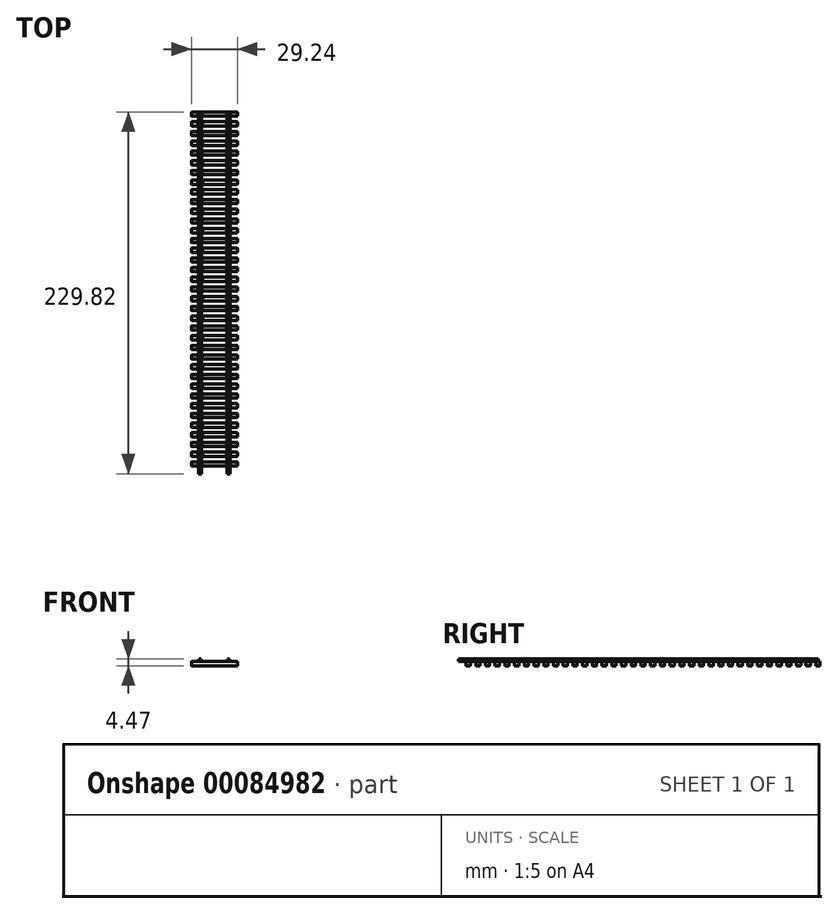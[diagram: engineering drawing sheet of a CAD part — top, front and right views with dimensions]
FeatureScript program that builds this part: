
annotation { "Feature Type Name" : "Feature", "Feature Type Description" : "" }
export const myFeature = defineFeature(function(context is Context, id is Id, definition is map)
    precondition{}
    {
        {
            var Q0;
            Q0=qCreatedBy(makeId("Top.planeOp"),FACE);
            var sketch = newSketch(context, id + "F0", { "sketchPlane" : qUnion([Q0])});
            skLineSegment(sketch, "E0.bottom", {"start": v(-14.62, 0) * mm, "end": v(14.62, 0) * mm});
            skLineSegment(sketch, "E0.top", {"start": v(-14.62, -2.7) * mm, "end": v(14.62, -2.7) * mm});
            skLineSegment(sketch, "E0.left", {"start": v(-14.62, 0) * mm, "end": v(-14.62, -2.7) * mm});
            skLineSegment(sketch, "E0.right", {"start": v(14.62, 0) * mm, "end": v(14.62, -2.7) * mm});
            skLineSegment(sketch, "E1.0.1.0", {"start": v(-14.62, 3.48) * mm, "end": v(14.62, 3.48) * mm});
            skLineSegment(sketch, "E1.0.1.1", {"start": v(-14.62, 6.17) * mm, "end": v(14.62, 6.17) * mm});
            skLineSegment(sketch, "E1.0.1.2", {"start": v(-14.62, 6.17) * mm, "end": v(-14.62, 3.48) * mm});
            skLineSegment(sketch, "E1.0.1.3", {"start": v(14.62, 6.17) * mm, "end": v(14.62, 3.48) * mm});
            skLineSegment(sketch, "E1.0.2.0", {"start": v(-14.62, 9.65) * mm, "end": v(14.62, 9.65) * mm});
            skLineSegment(sketch, "E1.0.2.1", {"start": v(-14.62, 12.34) * mm, "end": v(14.62, 12.34) * mm});
            skLineSegment(sketch, "E1.0.2.2", {"start": v(-14.62, 12.34) * mm, "end": v(-14.62, 9.65) * mm});
            skLineSegment(sketch, "E1.0.2.3", {"start": v(14.62, 12.34) * mm, "end": v(14.62, 9.65) * mm});
            skLineSegment(sketch, "E1.0.3.0", {"start": v(-14.62, 15.82) * mm, "end": v(14.62, 15.82) * mm});
            skLineSegment(sketch, "E1.0.3.1", {"start": v(-14.62, 18.52) * mm, "end": v(14.62, 18.52) * mm});
            skLineSegment(sketch, "E1.0.3.2", {"start": v(-14.62, 18.52) * mm, "end": v(-14.62, 15.82) * mm});
            skLineSegment(sketch, "E1.0.3.3", {"start": v(14.62, 18.52) * mm, "end": v(14.62, 15.82) * mm});
            skLineSegment(sketch, "E1.0.4.0", {"start": v(-14.62, 22) * mm, "end": v(14.62, 22) * mm});
            skLineSegment(sketch, "E1.0.4.1", {"start": v(-14.62, 24.69) * mm, "end": v(14.62, 24.69) * mm});
            skLineSegment(sketch, "E1.0.4.2", {"start": v(-14.62, 24.69) * mm, "end": v(-14.62, 22) * mm});
            skLineSegment(sketch, "E1.0.4.3", {"start": v(14.62, 24.69) * mm, "end": v(14.62, 22) * mm});
            skLineSegment(sketch, "E1.0.5.0", {"start": v(-14.62, 28.17) * mm, "end": v(14.62, 28.17) * mm});
            skLineSegment(sketch, "E1.0.5.1", {"start": v(-14.62, 30.86) * mm, "end": v(14.62, 30.86) * mm});
            skLineSegment(sketch, "E1.0.5.2", {"start": v(-14.62, 30.86) * mm, "end": v(-14.62, 28.17) * mm});
            skLineSegment(sketch, "E1.0.5.3", {"start": v(14.62, 30.86) * mm, "end": v(14.62, 28.17) * mm});
            skLineSegment(sketch, "E1.0.6.0", {"start": v(-14.62, 34.34) * mm, "end": v(14.62, 34.34) * mm});
            skLineSegment(sketch, "E1.0.6.1", {"start": v(-14.62, 37.03) * mm, "end": v(14.62, 37.03) * mm});
            skLineSegment(sketch, "E1.0.6.2", {"start": v(-14.62, 37.03) * mm, "end": v(-14.62, 34.34) * mm});
            skLineSegment(sketch, "E1.0.6.3", {"start": v(14.62, 37.03) * mm, "end": v(14.62, 34.34) * mm});
            skLineSegment(sketch, "E1.0.7.0", {"start": v(-14.62, 40.51) * mm, "end": v(14.62, 40.51) * mm});
            skLineSegment(sketch, "E1.0.7.1", {"start": v(-14.62, 43.2) * mm, "end": v(14.62, 43.2) * mm});
            skLineSegment(sketch, "E1.0.7.2", {"start": v(-14.62, 43.2) * mm, "end": v(-14.62, 40.51) * mm});
            skLineSegment(sketch, "E1.0.7.3", {"start": v(14.62, 43.2) * mm, "end": v(14.62, 40.51) * mm});
            skLineSegment(sketch, "E1.0.8.0", {"start": v(-14.62, 46.69) * mm, "end": v(14.62, 46.69) * mm});
            skLineSegment(sketch, "E1.0.8.1", {"start": v(-14.62, 49.38) * mm, "end": v(14.62, 49.38) * mm});
            skLineSegment(sketch, "E1.0.8.2", {"start": v(-14.62, 49.38) * mm, "end": v(-14.62, 46.69) * mm});
            skLineSegment(sketch, "E1.0.8.3", {"start": v(14.62, 49.38) * mm, "end": v(14.62, 46.69) * mm});
            skLineSegment(sketch, "E1.0.9.0", {"start": v(-14.62, 52.86) * mm, "end": v(14.62, 52.86) * mm});
            skLineSegment(sketch, "E1.0.9.1", {"start": v(-14.62, 55.55) * mm, "end": v(14.62, 55.55) * mm});
            skLineSegment(sketch, "E1.0.9.2", {"start": v(-14.62, 55.55) * mm, "end": v(-14.62, 52.86) * mm});
            skLineSegment(sketch, "E1.0.9.3", {"start": v(14.62, 55.55) * mm, "end": v(14.62, 52.86) * mm});
            skLineSegment(sketch, "E1.0.10.0", {"start": v(-14.62, 59.03) * mm, "end": v(14.62, 59.03) * mm});
            skLineSegment(sketch, "E1.0.10.1", {"start": v(-14.62, 61.72) * mm, "end": v(14.62, 61.72) * mm});
            skLineSegment(sketch, "E1.0.10.2", {"start": v(-14.62, 61.72) * mm, "end": v(-14.62, 59.03) * mm});
            skLineSegment(sketch, "E1.0.10.3", {"start": v(14.62, 61.72) * mm, "end": v(14.62, 59.03) * mm});
            skLineSegment(sketch, "E1.0.11.0", {"start": v(-14.62, 65.2) * mm, "end": v(14.62, 65.2) * mm});
            skLineSegment(sketch, "E1.0.11.1", {"start": v(-14.62, 67.9) * mm, "end": v(14.62, 67.9) * mm});
            skLineSegment(sketch, "E1.0.11.2", {"start": v(-14.62, 67.9) * mm, "end": v(-14.62, 65.2) * mm});
            skLineSegment(sketch, "E1.0.11.3", {"start": v(14.62, 67.9) * mm, "end": v(14.62, 65.2) * mm});
            skLineSegment(sketch, "E1.0.12.0", {"start": v(-14.62, 71.37) * mm, "end": v(14.62, 71.37) * mm});
            skLineSegment(sketch, "E1.0.12.1", {"start": v(-14.62, 74.07) * mm, "end": v(14.62, 74.07) * mm});
            skLineSegment(sketch, "E1.0.12.2", {"start": v(-14.62, 74.07) * mm, "end": v(-14.62, 71.37) * mm});
            skLineSegment(sketch, "E1.0.12.3", {"start": v(14.62, 74.07) * mm, "end": v(14.62, 71.37) * mm});
            skLineSegment(sketch, "E1.0.13.0", {"start": v(-14.62, 77.55) * mm, "end": v(14.62, 77.55) * mm});
            skLineSegment(sketch, "E1.0.13.1", {"start": v(-14.62, 80.24) * mm, "end": v(14.62, 80.24) * mm});
            skLineSegment(sketch, "E1.0.13.2", {"start": v(-14.62, 80.24) * mm, "end": v(-14.62, 77.55) * mm});
            skLineSegment(sketch, "E1.0.13.3", {"start": v(14.62, 80.24) * mm, "end": v(14.62, 77.55) * mm});
            skLineSegment(sketch, "E1.0.14.0", {"start": v(-14.62, 83.72) * mm, "end": v(14.62, 83.72) * mm});
            skLineSegment(sketch, "E1.0.14.1", {"start": v(-14.62, 86.41) * mm, "end": v(14.62, 86.41) * mm});
            skLineSegment(sketch, "E1.0.14.2", {"start": v(-14.62, 86.41) * mm, "end": v(-14.62, 83.72) * mm});
            skLineSegment(sketch, "E1.0.14.3", {"start": v(14.62, 86.41) * mm, "end": v(14.62, 83.72) * mm});
            skLineSegment(sketch, "E1.0.15.0", {"start": v(-14.62, 89.9) * mm, "end": v(14.62, 89.9) * mm});
            skLineSegment(sketch, "E1.0.15.1", {"start": v(-14.62, 92.58) * mm, "end": v(14.62, 92.58) * mm});
            skLineSegment(sketch, "E1.0.15.2", {"start": v(-14.62, 92.58) * mm, "end": v(-14.62, 89.9) * mm});
            skLineSegment(sketch, "E1.0.15.3", {"start": v(14.62, 92.58) * mm, "end": v(14.62, 89.9) * mm});
            skLineSegment(sketch, "E1.0.16.0", {"start": v(-14.62, 96.06) * mm, "end": v(14.62, 96.06) * mm});
            skLineSegment(sketch, "E1.0.16.1", {"start": v(-14.62, 98.76) * mm, "end": v(14.62, 98.76) * mm});
            skLineSegment(sketch, "E1.0.16.2", {"start": v(-14.62, 98.76) * mm, "end": v(-14.62, 96.06) * mm});
            skLineSegment(sketch, "E1.0.16.3", {"start": v(14.62, 98.76) * mm, "end": v(14.62, 96.06) * mm});
            skLineSegment(sketch, "E1.0.17.0", {"start": v(-14.62, 102.23) * mm, "end": v(14.62, 102.23) * mm});
            skLineSegment(sketch, "E1.0.17.1", {"start": v(-14.62, 104.93) * mm, "end": v(14.62, 104.93) * mm});
            skLineSegment(sketch, "E1.0.17.2", {"start": v(-14.62, 104.93) * mm, "end": v(-14.62, 102.23) * mm});
            skLineSegment(sketch, "E1.0.17.3", {"start": v(14.62, 104.93) * mm, "end": v(14.62, 102.23) * mm});
            skLineSegment(sketch, "E1.0.18.0", {"start": v(-14.62, 108.4) * mm, "end": v(14.62, 108.4) * mm});
            skLineSegment(sketch, "E1.0.18.1", {"start": v(-14.62, 111.1) * mm, "end": v(14.62, 111.1) * mm});
            skLineSegment(sketch, "E1.0.18.2", {"start": v(-14.62, 111.1) * mm, "end": v(-14.62, 108.4) * mm});
            skLineSegment(sketch, "E1.0.18.3", {"start": v(14.62, 111.1) * mm, "end": v(14.62, 108.4) * mm});
            skLineSegment(sketch, "E1.0.19.0", {"start": v(-14.62, 114.58) * mm, "end": v(14.62, 114.58) * mm});
            skLineSegment(sketch, "E1.0.19.1", {"start": v(-14.62, 117.27) * mm, "end": v(14.62, 117.27) * mm});
            skLineSegment(sketch, "E1.0.19.2", {"start": v(-14.62, 117.27) * mm, "end": v(-14.62, 114.58) * mm});
            skLineSegment(sketch, "E1.0.19.3", {"start": v(14.62, 117.27) * mm, "end": v(14.62, 114.58) * mm});
            skLineSegment(sketch, "E1.direction1", {"start": v(-14.62, -2.7) * mm, "end": v(10.4, -2.7) * mm, "construction": true});
            skLineSegment(sketch, "E1.direction2", {"start": v(-14.62, -2.7) * mm, "end": v(-14.62, 3.48) * mm, "construction": true});
            skLineSegment(sketch, "E2.0.0.20", {"start": v(-14.62, 120.75) * mm, "end": v(14.62, 120.75) * mm});
            skLineSegment(sketch, "E2.3.0.20", {"start": v(-14.62, 123.44) * mm, "end": v(14.62, 123.44) * mm});
            skLineSegment(sketch, "E2.6.0.20", {"start": v(-14.62, 123.44) * mm, "end": v(-14.62, 120.75) * mm});
            skLineSegment(sketch, "E2.9.0.20", {"start": v(14.62, 123.44) * mm, "end": v(14.62, 120.75) * mm});
            skLineSegment(sketch, "E2.0.0.21", {"start": v(-14.62, 126.92) * mm, "end": v(14.62, 126.92) * mm});
            skLineSegment(sketch, "E2.3.0.21", {"start": v(-14.62, 129.62) * mm, "end": v(14.62, 129.62) * mm});
            skLineSegment(sketch, "E2.6.0.21", {"start": v(-14.62, 129.62) * mm, "end": v(-14.62, 126.92) * mm});
            skLineSegment(sketch, "E2.9.0.21", {"start": v(14.62, 129.62) * mm, "end": v(14.62, 126.92) * mm});
            skLineSegment(sketch, "E2.0.0.22", {"start": v(-14.62, 133.1) * mm, "end": v(14.62, 133.1) * mm});
            skLineSegment(sketch, "E2.3.0.22", {"start": v(-14.62, 135.79) * mm, "end": v(14.62, 135.79) * mm});
            skLineSegment(sketch, "E2.6.0.22", {"start": v(-14.62, 135.79) * mm, "end": v(-14.62, 133.1) * mm});
            skLineSegment(sketch, "E2.9.0.22", {"start": v(14.62, 135.79) * mm, "end": v(14.62, 133.1) * mm});
            skLineSegment(sketch, "E2.0.0.23", {"start": v(-14.62, 139.27) * mm, "end": v(14.62, 139.27) * mm});
            skLineSegment(sketch, "E2.3.0.23", {"start": v(-14.62, 141.96) * mm, "end": v(14.62, 141.96) * mm});
            skLineSegment(sketch, "E2.6.0.23", {"start": v(-14.62, 141.96) * mm, "end": v(-14.62, 139.27) * mm});
            skLineSegment(sketch, "E2.9.0.23", {"start": v(14.62, 141.96) * mm, "end": v(14.62, 139.27) * mm});
            skLineSegment(sketch, "E2.0.0.24", {"start": v(-14.62, 145.44) * mm, "end": v(14.62, 145.44) * mm});
            skLineSegment(sketch, "E2.3.0.24", {"start": v(-14.62, 148.13) * mm, "end": v(14.62, 148.13) * mm});
            skLineSegment(sketch, "E2.6.0.24", {"start": v(-14.62, 148.13) * mm, "end": v(-14.62, 145.44) * mm});
            skLineSegment(sketch, "E2.9.0.24", {"start": v(14.62, 148.13) * mm, "end": v(14.62, 145.44) * mm});
            skLineSegment(sketch, "E2.0.0.25", {"start": v(-14.62, 151.61) * mm, "end": v(14.62, 151.61) * mm});
            skLineSegment(sketch, "E2.3.0.25", {"start": v(-14.62, 154.3) * mm, "end": v(14.62, 154.3) * mm});
            skLineSegment(sketch, "E2.6.0.25", {"start": v(-14.62, 154.3) * mm, "end": v(-14.62, 151.61) * mm});
            skLineSegment(sketch, "E2.9.0.25", {"start": v(14.62, 154.3) * mm, "end": v(14.62, 151.61) * mm});
            skLineSegment(sketch, "E2.0.0.26", {"start": v(-14.62, 157.78) * mm, "end": v(14.62, 157.78) * mm});
            skLineSegment(sketch, "E2.3.0.26", {"start": v(-14.62, 160.48) * mm, "end": v(14.62, 160.48) * mm});
            skLineSegment(sketch, "E2.6.0.26", {"start": v(-14.62, 160.48) * mm, "end": v(-14.62, 157.78) * mm});
            skLineSegment(sketch, "E2.9.0.26", {"start": v(14.62, 160.48) * mm, "end": v(14.62, 157.78) * mm});
            skLineSegment(sketch, "E2.0.0.27", {"start": v(-14.62, 163.96) * mm, "end": v(14.62, 163.96) * mm});
            skLineSegment(sketch, "E2.3.0.27", {"start": v(-14.62, 166.65) * mm, "end": v(14.62, 166.65) * mm});
            skLineSegment(sketch, "E2.6.0.27", {"start": v(-14.62, 166.65) * mm, "end": v(-14.62, 163.96) * mm});
            skLineSegment(sketch, "E2.9.0.27", {"start": v(14.62, 166.65) * mm, "end": v(14.62, 163.96) * mm});
            skLineSegment(sketch, "E2.0.0.28", {"start": v(-14.62, 170.13) * mm, "end": v(14.62, 170.13) * mm});
            skLineSegment(sketch, "E2.3.0.28", {"start": v(-14.62, 172.82) * mm, "end": v(14.62, 172.82) * mm});
            skLineSegment(sketch, "E2.6.0.28", {"start": v(-14.62, 172.82) * mm, "end": v(-14.62, 170.13) * mm});
            skLineSegment(sketch, "E2.9.0.28", {"start": v(14.62, 172.82) * mm, "end": v(14.62, 170.13) * mm});
            skLineSegment(sketch, "E2.0.0.29", {"start": v(-14.62, 176.3) * mm, "end": v(14.62, 176.3) * mm});
            skLineSegment(sketch, "E2.3.0.29", {"start": v(-14.62, 179) * mm, "end": v(14.62, 179) * mm});
            skLineSegment(sketch, "E2.6.0.29", {"start": v(-14.62, 179) * mm, "end": v(-14.62, 176.3) * mm});
            skLineSegment(sketch, "E2.9.0.29", {"start": v(14.62, 179) * mm, "end": v(14.62, 176.3) * mm});
            skLineSegment(sketch, "E3.0.0.30", {"start": v(-14.62, 182.47) * mm, "end": v(14.62, 182.47) * mm});
            skLineSegment(sketch, "E3.3.0.30", {"start": v(-14.62, 185.17) * mm, "end": v(14.62, 185.17) * mm});
            skLineSegment(sketch, "E3.6.0.30", {"start": v(-14.62, 185.17) * mm, "end": v(-14.62, 182.47) * mm});
            skLineSegment(sketch, "E3.9.0.30", {"start": v(14.62, 185.17) * mm, "end": v(14.62, 182.47) * mm});
            skLineSegment(sketch, "E3.0.0.31", {"start": v(-14.62, 188.65) * mm, "end": v(14.62, 188.65) * mm});
            skLineSegment(sketch, "E3.3.0.31", {"start": v(-14.62, 191.34) * mm, "end": v(14.62, 191.34) * mm});
            skLineSegment(sketch, "E3.6.0.31", {"start": v(-14.62, 191.34) * mm, "end": v(-14.62, 188.65) * mm});
            skLineSegment(sketch, "E3.9.0.31", {"start": v(14.62, 191.34) * mm, "end": v(14.62, 188.65) * mm});
            skLineSegment(sketch, "E3.0.0.32", {"start": v(-14.62, 194.82) * mm, "end": v(14.62, 194.82) * mm});
            skLineSegment(sketch, "E3.3.0.32", {"start": v(-14.62, 197.51) * mm, "end": v(14.62, 197.51) * mm});
            skLineSegment(sketch, "E3.6.0.32", {"start": v(-14.62, 197.51) * mm, "end": v(-14.62, 194.82) * mm});
            skLineSegment(sketch, "E3.9.0.32", {"start": v(14.62, 197.51) * mm, "end": v(14.62, 194.82) * mm});
            skLineSegment(sketch, "E3.0.0.33", {"start": v(-14.62, 201) * mm, "end": v(14.62, 201) * mm});
            skLineSegment(sketch, "E3.3.0.33", {"start": v(-14.62, 203.68) * mm, "end": v(14.62, 203.68) * mm});
            skLineSegment(sketch, "E3.6.0.33", {"start": v(-14.62, 203.68) * mm, "end": v(-14.62, 201) * mm});
            skLineSegment(sketch, "E3.9.0.33", {"start": v(14.62, 203.68) * mm, "end": v(14.62, 201) * mm});
            skLineSegment(sketch, "E3.0.0.34", {"start": v(-14.62, 207.16) * mm, "end": v(14.62, 207.16) * mm});
            skLineSegment(sketch, "E3.3.0.34", {"start": v(-14.62, 209.85) * mm, "end": v(14.62, 209.85) * mm});
            skLineSegment(sketch, "E3.6.0.34", {"start": v(-14.62, 209.85) * mm, "end": v(-14.62, 207.16) * mm});
            skLineSegment(sketch, "E3.9.0.34", {"start": v(14.62, 209.85) * mm, "end": v(14.62, 207.16) * mm});
            skLineSegment(sketch, "E3.0.0.35", {"start": v(-14.62, 213.33) * mm, "end": v(14.62, 213.33) * mm});
            skLineSegment(sketch, "E3.3.0.35", {"start": v(-14.62, 216.03) * mm, "end": v(14.62, 216.03) * mm});
            skLineSegment(sketch, "E3.6.0.35", {"start": v(-14.62, 216.03) * mm, "end": v(-14.62, 213.33) * mm});
            skLineSegment(sketch, "E3.9.0.35", {"start": v(14.62, 216.03) * mm, "end": v(14.62, 213.33) * mm});
            skLineSegment(sketch, "E3.0.0.36", {"start": v(-14.62, 219.5) * mm, "end": v(14.62, 219.5) * mm});
            skLineSegment(sketch, "E3.3.0.36", {"start": v(-14.62, 222.2) * mm, "end": v(14.62, 222.2) * mm});
            skLineSegment(sketch, "E3.6.0.36", {"start": v(-14.62, 222.2) * mm, "end": v(-14.62, 219.5) * mm});
            skLineSegment(sketch, "E3.9.0.36", {"start": v(14.62, 222.2) * mm, "end": v(14.62, 219.5) * mm});
            skSolve(sketch);
        }
        {
            var Q0;
            Q0 = qSketchRegion(id + "F0", true);
            extrude(context, id + "F1", {"entities" : qUnion([Q0]), "depth" : 2.7 * mm});
        }
        {
            var Q0;
            Q0=makeQuery(id+"F1.opExtrude","CAP_FACE",FACE,{"disambiguationData":[OSD([sQuery(id+"F0.wireOp",EDGE,"E0.bottom"),sQuery(id+"F0.wireOp",EDGE,"E0.top"),sQuery(id+"F0.wireOp",EDGE,"E0.left"),sQuery(id+"F0.wireOp",EDGE,"E0.right")])],"isStart":false});
            var Q1;
            Q1=makeQuery(id+"F1.opExtrude","CAP_FACE",FACE,{"disambiguationData":[OSD([sQuery(id+"F0.wireOp",EDGE,"E1.0.1.0"),sQuery(id+"F0.wireOp",EDGE,"E1.0.1.1"),sQuery(id+"F0.wireOp",EDGE,"E1.0.1.2"),sQuery(id+"F0.wireOp",EDGE,"E1.0.1.3")])],"isStart":false});
            var Q2;
            Q2=makeQuery(id+"F1.opExtrude","CAP_FACE",FACE,{"disambiguationData":[OSD([sQuery(id+"F0.wireOp",EDGE,"E1.0.2.0"),sQuery(id+"F0.wireOp",EDGE,"E1.0.2.1"),sQuery(id+"F0.wireOp",EDGE,"E1.0.2.2"),sQuery(id+"F0.wireOp",EDGE,"E1.0.2.3")])],"isStart":false});
            var Q3;
            Q3=makeQuery(id+"F1.opExtrude","CAP_FACE",FACE,{"disambiguationData":[OSD([sQuery(id+"F0.wireOp",EDGE,"E1.0.3.0"),sQuery(id+"F0.wireOp",EDGE,"E1.0.3.1"),sQuery(id+"F0.wireOp",EDGE,"E1.0.3.2"),sQuery(id+"F0.wireOp",EDGE,"E1.0.3.3")])],"isStart":false});
            var Q4;
            Q4=makeQuery(id+"F1.opExtrude","CAP_FACE",FACE,{"disambiguationData":[OSD([sQuery(id+"F0.wireOp",EDGE,"E1.0.4.0"),sQuery(id+"F0.wireOp",EDGE,"E1.0.4.1"),sQuery(id+"F0.wireOp",EDGE,"E1.0.4.2"),sQuery(id+"F0.wireOp",EDGE,"E1.0.4.3")])],"isStart":false});
            var Q5;
            Q5=makeQuery(id+"F1.opExtrude","CAP_FACE",FACE,{"disambiguationData":[OSD([sQuery(id+"F0.wireOp",EDGE,"E1.0.5.0"),sQuery(id+"F0.wireOp",EDGE,"E1.0.5.1"),sQuery(id+"F0.wireOp",EDGE,"E1.0.5.2"),sQuery(id+"F0.wireOp",EDGE,"E1.0.5.3")])],"isStart":false});
            var Q6;
            Q6=makeQuery(id+"F1.opExtrude","CAP_FACE",FACE,{"disambiguationData":[OSD([sQuery(id+"F0.wireOp",EDGE,"E1.0.6.0"),sQuery(id+"F0.wireOp",EDGE,"E1.0.6.1"),sQuery(id+"F0.wireOp",EDGE,"E1.0.6.2"),sQuery(id+"F0.wireOp",EDGE,"E1.0.6.3")])],"isStart":false});
            var Q7;
            Q7=makeQuery(id+"F1.opExtrude","CAP_FACE",FACE,{"disambiguationData":[OSD([sQuery(id+"F0.wireOp",EDGE,"E1.0.7.0"),sQuery(id+"F0.wireOp",EDGE,"E1.0.7.1"),sQuery(id+"F0.wireOp",EDGE,"E1.0.7.2"),sQuery(id+"F0.wireOp",EDGE,"E1.0.7.3")])],"isStart":false});
            var Q8;
            Q8=makeQuery(id+"F1.opExtrude","CAP_FACE",FACE,{"disambiguationData":[OSD([sQuery(id+"F0.wireOp",EDGE,"E1.0.8.0"),sQuery(id+"F0.wireOp",EDGE,"E1.0.8.1"),sQuery(id+"F0.wireOp",EDGE,"E1.0.8.2"),sQuery(id+"F0.wireOp",EDGE,"E1.0.8.3")])],"isStart":false});
            var Q9;
            Q9=makeQuery(id+"F1.opExtrude","CAP_FACE",FACE,{"disambiguationData":[OSD([sQuery(id+"F0.wireOp",EDGE,"E1.0.9.0"),sQuery(id+"F0.wireOp",EDGE,"E1.0.9.1"),sQuery(id+"F0.wireOp",EDGE,"E1.0.9.2"),sQuery(id+"F0.wireOp",EDGE,"E1.0.9.3")])],"isStart":false});
            var Q10;
            Q10=makeQuery(id+"F1.opExtrude","CAP_FACE",FACE,{"disambiguationData":[OSD([sQuery(id+"F0.wireOp",EDGE,"E1.0.10.0"),sQuery(id+"F0.wireOp",EDGE,"E1.0.10.1"),sQuery(id+"F0.wireOp",EDGE,"E1.0.10.2"),sQuery(id+"F0.wireOp",EDGE,"E1.0.10.3")])],"isStart":false});
            var Q11;
            Q11=makeQuery(id+"F1.opExtrude","CAP_FACE",FACE,{"disambiguationData":[OSD([sQuery(id+"F0.wireOp",EDGE,"E1.0.11.0"),sQuery(id+"F0.wireOp",EDGE,"E1.0.11.1"),sQuery(id+"F0.wireOp",EDGE,"E1.0.11.2"),sQuery(id+"F0.wireOp",EDGE,"E1.0.11.3")])],"isStart":false});
            var Q12;
            Q12=makeQuery(id+"F1.opExtrude","CAP_FACE",FACE,{"disambiguationData":[OSD([sQuery(id+"F0.wireOp",EDGE,"E1.0.12.0"),sQuery(id+"F0.wireOp",EDGE,"E1.0.12.1"),sQuery(id+"F0.wireOp",EDGE,"E1.0.12.2"),sQuery(id+"F0.wireOp",EDGE,"E1.0.12.3")])],"isStart":false});
            var Q13;
            Q13=makeQuery(id+"F1.opExtrude","CAP_FACE",FACE,{"disambiguationData":[OSD([sQuery(id+"F0.wireOp",EDGE,"E1.0.13.0"),sQuery(id+"F0.wireOp",EDGE,"E1.0.13.1"),sQuery(id+"F0.wireOp",EDGE,"E1.0.13.2"),sQuery(id+"F0.wireOp",EDGE,"E1.0.13.3")])],"isStart":false});
            var Q14;
            Q14=makeQuery(id+"F1.opExtrude","CAP_FACE",FACE,{"disambiguationData":[OSD([sQuery(id+"F0.wireOp",EDGE,"E1.0.14.0"),sQuery(id+"F0.wireOp",EDGE,"E1.0.14.1"),sQuery(id+"F0.wireOp",EDGE,"E1.0.14.2"),sQuery(id+"F0.wireOp",EDGE,"E1.0.14.3")])],"isStart":false});
            var Q15;
            Q15=makeQuery(id+"F1.opExtrude","CAP_FACE",FACE,{"disambiguationData":[OSD([sQuery(id+"F0.wireOp",EDGE,"E1.0.15.0"),sQuery(id+"F0.wireOp",EDGE,"E1.0.15.1"),sQuery(id+"F0.wireOp",EDGE,"E1.0.15.2"),sQuery(id+"F0.wireOp",EDGE,"E1.0.15.3")])],"isStart":false});
            var Q16;
            Q16=makeQuery(id+"F1.opExtrude","CAP_FACE",FACE,{"disambiguationData":[OSD([sQuery(id+"F0.wireOp",EDGE,"E1.0.17.0"),sQuery(id+"F0.wireOp",EDGE,"E1.0.17.1"),sQuery(id+"F0.wireOp",EDGE,"E1.0.17.2"),sQuery(id+"F0.wireOp",EDGE,"E1.0.17.3")])],"isStart":false});
            var Q17;
            Q17=makeQuery(id+"F1.opExtrude","CAP_FACE",FACE,{"disambiguationData":[OSD([sQuery(id+"F0.wireOp",EDGE,"E1.0.18.0"),sQuery(id+"F0.wireOp",EDGE,"E1.0.18.1"),sQuery(id+"F0.wireOp",EDGE,"E1.0.18.2"),sQuery(id+"F0.wireOp",EDGE,"E1.0.18.3")])],"isStart":false});
            var Q18;
            Q18=makeQuery(id+"F1.opExtrude","CAP_FACE",FACE,{"disambiguationData":[OSD([sQuery(id+"F0.wireOp",EDGE,"E1.0.19.0"),sQuery(id+"F0.wireOp",EDGE,"E1.0.19.1"),sQuery(id+"F0.wireOp",EDGE,"E1.0.19.2"),sQuery(id+"F0.wireOp",EDGE,"E1.0.19.3")])],"isStart":false});
            var Q19;
            Q19=makeQuery(id+"F1.opExtrude","CAP_FACE",FACE,{"disambiguationData":[OSD([sQuery(id+"F0.wireOp",EDGE,"E2.0.0.20"),sQuery(id+"F0.wireOp",EDGE,"E2.3.0.20"),sQuery(id+"F0.wireOp",EDGE,"E2.6.0.20"),sQuery(id+"F0.wireOp",EDGE,"E2.9.0.20")])],"isStart":false});
            var Q20;
            Q20=makeQuery(id+"F1.opExtrude","CAP_FACE",FACE,{"disambiguationData":[OSD([sQuery(id+"F0.wireOp",EDGE,"E2.0.0.21"),sQuery(id+"F0.wireOp",EDGE,"E2.3.0.21"),sQuery(id+"F0.wireOp",EDGE,"E2.6.0.21"),sQuery(id+"F0.wireOp",EDGE,"E2.9.0.21")])],"isStart":false});
            var Q21;
            Q21=makeQuery(id+"F1.opExtrude","CAP_FACE",FACE,{"disambiguationData":[OSD([sQuery(id+"F0.wireOp",EDGE,"E2.0.0.22"),sQuery(id+"F0.wireOp",EDGE,"E2.3.0.22"),sQuery(id+"F0.wireOp",EDGE,"E2.6.0.22"),sQuery(id+"F0.wireOp",EDGE,"E2.9.0.22")])],"isStart":false});
            var Q22;
            Q22=makeQuery(id+"F1.opExtrude","CAP_FACE",FACE,{"disambiguationData":[OSD([sQuery(id+"F0.wireOp",EDGE,"E2.0.0.23"),sQuery(id+"F0.wireOp",EDGE,"E2.3.0.23"),sQuery(id+"F0.wireOp",EDGE,"E2.6.0.23"),sQuery(id+"F0.wireOp",EDGE,"E2.9.0.23")])],"isStart":false});
            var Q23;
            Q23=makeQuery(id+"F1.opExtrude","CAP_FACE",FACE,{"disambiguationData":[OSD([sQuery(id+"F0.wireOp",EDGE,"E2.0.0.24"),sQuery(id+"F0.wireOp",EDGE,"E2.3.0.24"),sQuery(id+"F0.wireOp",EDGE,"E2.6.0.24"),sQuery(id+"F0.wireOp",EDGE,"E2.9.0.24")])],"isStart":false});
            var Q24;
            Q24=makeQuery(id+"F1.opExtrude","CAP_FACE",FACE,{"disambiguationData":[OSD([sQuery(id+"F0.wireOp",EDGE,"E2.0.0.25"),sQuery(id+"F0.wireOp",EDGE,"E2.3.0.25"),sQuery(id+"F0.wireOp",EDGE,"E2.6.0.25"),sQuery(id+"F0.wireOp",EDGE,"E2.9.0.25")])],"isStart":false});
            var Q25;
            Q25=makeQuery(id+"F1.opExtrude","CAP_FACE",FACE,{"disambiguationData":[OSD([sQuery(id+"F0.wireOp",EDGE,"E2.0.0.26"),sQuery(id+"F0.wireOp",EDGE,"E2.3.0.26"),sQuery(id+"F0.wireOp",EDGE,"E2.6.0.26"),sQuery(id+"F0.wireOp",EDGE,"E2.9.0.26")])],"isStart":false});
            var Q26;
            Q26=makeQuery(id+"F1.opExtrude","CAP_FACE",FACE,{"disambiguationData":[OSD([sQuery(id+"F0.wireOp",EDGE,"E2.0.0.27"),sQuery(id+"F0.wireOp",EDGE,"E2.3.0.27"),sQuery(id+"F0.wireOp",EDGE,"E2.6.0.27"),sQuery(id+"F0.wireOp",EDGE,"E2.9.0.27")])],"isStart":false});
            var Q27;
            Q27=makeQuery(id+"F1.opExtrude","CAP_FACE",FACE,{"disambiguationData":[OSD([sQuery(id+"F0.wireOp",EDGE,"E2.0.0.28"),sQuery(id+"F0.wireOp",EDGE,"E2.3.0.28"),sQuery(id+"F0.wireOp",EDGE,"E2.6.0.28"),sQuery(id+"F0.wireOp",EDGE,"E2.9.0.28")])],"isStart":false});
            var Q28;
            Q28=makeQuery(id+"F1.opExtrude","CAP_FACE",FACE,{"disambiguationData":[OSD([sQuery(id+"F0.wireOp",EDGE,"E2.0.0.29"),sQuery(id+"F0.wireOp",EDGE,"E2.3.0.29"),sQuery(id+"F0.wireOp",EDGE,"E2.6.0.29"),sQuery(id+"F0.wireOp",EDGE,"E2.9.0.29")])],"isStart":false});
            var Q29;
            Q29=makeQuery(id+"F1.opExtrude","CAP_FACE",FACE,{"disambiguationData":[OSD([sQuery(id+"F0.wireOp",EDGE,"E3.0.0.30"),sQuery(id+"F0.wireOp",EDGE,"E3.3.0.30"),sQuery(id+"F0.wireOp",EDGE,"E3.6.0.30"),sQuery(id+"F0.wireOp",EDGE,"E3.9.0.30")])],"isStart":false});
            var Q30;
            Q30=makeQuery(id+"F1.opExtrude","CAP_FACE",FACE,{"disambiguationData":[OSD([sQuery(id+"F0.wireOp",EDGE,"E3.0.0.31"),sQuery(id+"F0.wireOp",EDGE,"E3.3.0.31"),sQuery(id+"F0.wireOp",EDGE,"E3.6.0.31"),sQuery(id+"F0.wireOp",EDGE,"E3.9.0.31")])],"isStart":false});
            var Q31;
            Q31=makeQuery(id+"F1.opExtrude","CAP_FACE",FACE,{"disambiguationData":[OSD([sQuery(id+"F0.wireOp",EDGE,"E3.0.0.32"),sQuery(id+"F0.wireOp",EDGE,"E3.3.0.32"),sQuery(id+"F0.wireOp",EDGE,"E3.6.0.32"),sQuery(id+"F0.wireOp",EDGE,"E3.9.0.32")])],"isStart":false});
            var Q32;
            Q32=makeQuery(id+"F1.opExtrude","CAP_FACE",FACE,{"disambiguationData":[OSD([sQuery(id+"F0.wireOp",EDGE,"E3.0.0.33"),sQuery(id+"F0.wireOp",EDGE,"E3.3.0.33"),sQuery(id+"F0.wireOp",EDGE,"E3.6.0.33"),sQuery(id+"F0.wireOp",EDGE,"E3.9.0.33")])],"isStart":false});
            var Q33;
            Q33=makeQuery(id+"F1.opExtrude","CAP_FACE",FACE,{"disambiguationData":[OSD([sQuery(id+"F0.wireOp",EDGE,"E3.0.0.34"),sQuery(id+"F0.wireOp",EDGE,"E3.3.0.34"),sQuery(id+"F0.wireOp",EDGE,"E3.6.0.34"),sQuery(id+"F0.wireOp",EDGE,"E3.9.0.34")])],"isStart":false});
            var Q34;
            Q34=makeQuery(id+"F1.opExtrude","CAP_FACE",FACE,{"disambiguationData":[OSD([sQuery(id+"F0.wireOp",EDGE,"E3.0.0.35"),sQuery(id+"F0.wireOp",EDGE,"E3.3.0.35"),sQuery(id+"F0.wireOp",EDGE,"E3.6.0.35"),sQuery(id+"F0.wireOp",EDGE,"E3.9.0.35")])],"isStart":false});
            var Q35;
            Q35=makeQuery(id+"F1.opExtrude","CAP_FACE",FACE,{"disambiguationData":[OSD([sQuery(id+"F0.wireOp",EDGE,"E3.0.0.36"),sQuery(id+"F0.wireOp",EDGE,"E3.3.0.36"),sQuery(id+"F0.wireOp",EDGE,"E3.6.0.36"),sQuery(id+"F0.wireOp",EDGE,"E3.9.0.36")])],"isStart":false});
            var Q36;
            Q36=makeQuery(id+"F1.opExtrude","CAP_FACE",FACE,{"disambiguationData":[OSD([sQuery(id+"F0.wireOp",EDGE,"E1.0.1.0"),sQuery(id+"F0.wireOp",EDGE,"E1.0.1.1"),sQuery(id+"F0.wireOp",EDGE,"E1.0.1.2"),sQuery(id+"F0.wireOp",EDGE,"E1.0.1.3")])],"isStart":true});
            var Q37;
            Q37=makeQuery(id+"F1.opExtrude","CAP_FACE",FACE,{"disambiguationData":[OSD([sQuery(id+"F0.wireOp",EDGE,"E1.0.2.0"),sQuery(id+"F0.wireOp",EDGE,"E1.0.2.1"),sQuery(id+"F0.wireOp",EDGE,"E1.0.2.2"),sQuery(id+"F0.wireOp",EDGE,"E1.0.2.3")])],"isStart":true});
            var Q38;
            Q38=makeQuery(id+"F1.opExtrude","CAP_FACE",FACE,{"disambiguationData":[OSD([sQuery(id+"F0.wireOp",EDGE,"E1.0.3.0"),sQuery(id+"F0.wireOp",EDGE,"E1.0.3.1"),sQuery(id+"F0.wireOp",EDGE,"E1.0.3.2"),sQuery(id+"F0.wireOp",EDGE,"E1.0.3.3")])],"isStart":true});
            var Q39;
            Q39=makeQuery(id+"F1.opExtrude","CAP_FACE",FACE,{"disambiguationData":[OSD([sQuery(id+"F0.wireOp",EDGE,"E1.0.4.0"),sQuery(id+"F0.wireOp",EDGE,"E1.0.4.1"),sQuery(id+"F0.wireOp",EDGE,"E1.0.4.2"),sQuery(id+"F0.wireOp",EDGE,"E1.0.4.3")])],"isStart":true});
            var Q40;
            Q40=makeQuery(id+"F1.opExtrude","CAP_FACE",FACE,{"disambiguationData":[OSD([sQuery(id+"F0.wireOp",EDGE,"E1.0.5.0"),sQuery(id+"F0.wireOp",EDGE,"E1.0.5.1"),sQuery(id+"F0.wireOp",EDGE,"E1.0.5.2"),sQuery(id+"F0.wireOp",EDGE,"E1.0.5.3")])],"isStart":true});
            var Q41;
            Q41=makeQuery(id+"F1.opExtrude","CAP_FACE",FACE,{"disambiguationData":[OSD([sQuery(id+"F0.wireOp",EDGE,"E1.0.6.0"),sQuery(id+"F0.wireOp",EDGE,"E1.0.6.1"),sQuery(id+"F0.wireOp",EDGE,"E1.0.6.2"),sQuery(id+"F0.wireOp",EDGE,"E1.0.6.3")])],"isStart":true});
            var Q42;
            Q42=makeQuery(id+"F1.opExtrude","CAP_FACE",FACE,{"disambiguationData":[OSD([sQuery(id+"F0.wireOp",EDGE,"E1.0.7.0"),sQuery(id+"F0.wireOp",EDGE,"E1.0.7.1"),sQuery(id+"F0.wireOp",EDGE,"E1.0.7.2"),sQuery(id+"F0.wireOp",EDGE,"E1.0.7.3")])],"isStart":true});
            var Q43;
            Q43=makeQuery(id+"F1.opExtrude","CAP_FACE",FACE,{"disambiguationData":[OSD([sQuery(id+"F0.wireOp",EDGE,"E1.0.8.0"),sQuery(id+"F0.wireOp",EDGE,"E1.0.8.1"),sQuery(id+"F0.wireOp",EDGE,"E1.0.8.2"),sQuery(id+"F0.wireOp",EDGE,"E1.0.8.3")])],"isStart":true});
            var Q44;
            Q44=makeQuery(id+"F1.opExtrude","CAP_FACE",FACE,{"disambiguationData":[OSD([sQuery(id+"F0.wireOp",EDGE,"E1.0.9.0"),sQuery(id+"F0.wireOp",EDGE,"E1.0.9.1"),sQuery(id+"F0.wireOp",EDGE,"E1.0.9.2"),sQuery(id+"F0.wireOp",EDGE,"E1.0.9.3")])],"isStart":true});
            var Q45;
            Q45=makeQuery(id+"F1.opExtrude","CAP_FACE",FACE,{"disambiguationData":[OSD([sQuery(id+"F0.wireOp",EDGE,"E1.0.10.0"),sQuery(id+"F0.wireOp",EDGE,"E1.0.10.1"),sQuery(id+"F0.wireOp",EDGE,"E1.0.10.2"),sQuery(id+"F0.wireOp",EDGE,"E1.0.10.3")])],"isStart":true});
            var Q46;
            Q46=makeQuery(id+"F1.opExtrude","CAP_FACE",FACE,{"disambiguationData":[OSD([sQuery(id+"F0.wireOp",EDGE,"E1.0.11.0"),sQuery(id+"F0.wireOp",EDGE,"E1.0.11.1"),sQuery(id+"F0.wireOp",EDGE,"E1.0.11.2"),sQuery(id+"F0.wireOp",EDGE,"E1.0.11.3")])],"isStart":true});
            var Q47;
            Q47=makeQuery(id+"F1.opExtrude","CAP_FACE",FACE,{"disambiguationData":[OSD([sQuery(id+"F0.wireOp",EDGE,"E1.0.12.0"),sQuery(id+"F0.wireOp",EDGE,"E1.0.12.1"),sQuery(id+"F0.wireOp",EDGE,"E1.0.12.2"),sQuery(id+"F0.wireOp",EDGE,"E1.0.12.3")])],"isStart":true});
            var Q48;
            Q48=makeQuery(id+"F1.opExtrude","CAP_FACE",FACE,{"disambiguationData":[OSD([sQuery(id+"F0.wireOp",EDGE,"E1.0.13.0"),sQuery(id+"F0.wireOp",EDGE,"E1.0.13.1"),sQuery(id+"F0.wireOp",EDGE,"E1.0.13.2"),sQuery(id+"F0.wireOp",EDGE,"E1.0.13.3")])],"isStart":true});
            var Q49;
            Q49=makeQuery(id+"F1.opExtrude","CAP_FACE",FACE,{"disambiguationData":[OSD([sQuery(id+"F0.wireOp",EDGE,"E1.0.14.0"),sQuery(id+"F0.wireOp",EDGE,"E1.0.14.1"),sQuery(id+"F0.wireOp",EDGE,"E1.0.14.2"),sQuery(id+"F0.wireOp",EDGE,"E1.0.14.3")])],"isStart":true});
            var Q50;
            Q50=makeQuery(id+"F1.opExtrude","CAP_FACE",FACE,{"disambiguationData":[OSD([sQuery(id+"F0.wireOp",EDGE,"E1.0.15.0"),sQuery(id+"F0.wireOp",EDGE,"E1.0.15.1"),sQuery(id+"F0.wireOp",EDGE,"E1.0.15.2"),sQuery(id+"F0.wireOp",EDGE,"E1.0.15.3")])],"isStart":true});
            var Q51;
            Q51=makeQuery(id+"F1.opExtrude","CAP_FACE",FACE,{"disambiguationData":[OSD([sQuery(id+"F0.wireOp",EDGE,"E1.0.16.0"),sQuery(id+"F0.wireOp",EDGE,"E1.0.16.1"),sQuery(id+"F0.wireOp",EDGE,"E1.0.16.2"),sQuery(id+"F0.wireOp",EDGE,"E1.0.16.3")])],"isStart":true});
            var Q52;
            Q52=makeQuery(id+"F1.opExtrude","CAP_FACE",FACE,{"disambiguationData":[OSD([sQuery(id+"F0.wireOp",EDGE,"E1.0.17.0"),sQuery(id+"F0.wireOp",EDGE,"E1.0.17.1"),sQuery(id+"F0.wireOp",EDGE,"E1.0.17.2"),sQuery(id+"F0.wireOp",EDGE,"E1.0.17.3")])],"isStart":true});
            var Q53;
            Q53=makeQuery(id+"F1.opExtrude","CAP_FACE",FACE,{"disambiguationData":[OSD([sQuery(id+"F0.wireOp",EDGE,"E1.0.18.0"),sQuery(id+"F0.wireOp",EDGE,"E1.0.18.1"),sQuery(id+"F0.wireOp",EDGE,"E1.0.18.2"),sQuery(id+"F0.wireOp",EDGE,"E1.0.18.3")])],"isStart":true});
            var Q54;
            Q54=makeQuery(id+"F1.opExtrude","CAP_FACE",FACE,{"disambiguationData":[OSD([sQuery(id+"F0.wireOp",EDGE,"E2.0.0.21"),sQuery(id+"F0.wireOp",EDGE,"E2.3.0.21"),sQuery(id+"F0.wireOp",EDGE,"E2.6.0.21"),sQuery(id+"F0.wireOp",EDGE,"E2.9.0.21")])],"isStart":true});
            var Q55;
            Q55=makeQuery(id+"F1.opExtrude","CAP_FACE",FACE,{"disambiguationData":[OSD([sQuery(id+"F0.wireOp",EDGE,"E2.0.0.22"),sQuery(id+"F0.wireOp",EDGE,"E2.3.0.22"),sQuery(id+"F0.wireOp",EDGE,"E2.6.0.22"),sQuery(id+"F0.wireOp",EDGE,"E2.9.0.22")])],"isStart":true});
            var Q56;
            Q56=makeQuery(id+"F1.opExtrude","CAP_FACE",FACE,{"disambiguationData":[OSD([sQuery(id+"F0.wireOp",EDGE,"E2.0.0.23"),sQuery(id+"F0.wireOp",EDGE,"E2.3.0.23"),sQuery(id+"F0.wireOp",EDGE,"E2.6.0.23"),sQuery(id+"F0.wireOp",EDGE,"E2.9.0.23")])],"isStart":true});
            var Q57;
            Q57=makeQuery(id+"F1.opExtrude","CAP_FACE",FACE,{"disambiguationData":[OSD([sQuery(id+"F0.wireOp",EDGE,"E2.0.0.24"),sQuery(id+"F0.wireOp",EDGE,"E2.3.0.24"),sQuery(id+"F0.wireOp",EDGE,"E2.6.0.24"),sQuery(id+"F0.wireOp",EDGE,"E2.9.0.24")])],"isStart":true});
            var Q58;
            Q58=makeQuery(id+"F1.opExtrude","CAP_FACE",FACE,{"disambiguationData":[OSD([sQuery(id+"F0.wireOp",EDGE,"E2.0.0.25"),sQuery(id+"F0.wireOp",EDGE,"E2.3.0.25"),sQuery(id+"F0.wireOp",EDGE,"E2.6.0.25"),sQuery(id+"F0.wireOp",EDGE,"E2.9.0.25")])],"isStart":true});
            var Q59;
            Q59=makeQuery(id+"F1.opExtrude","CAP_FACE",FACE,{"disambiguationData":[OSD([sQuery(id+"F0.wireOp",EDGE,"E2.0.0.26"),sQuery(id+"F0.wireOp",EDGE,"E2.3.0.26"),sQuery(id+"F0.wireOp",EDGE,"E2.6.0.26"),sQuery(id+"F0.wireOp",EDGE,"E2.9.0.26")])],"isStart":true});
            var Q60;
            Q60=makeQuery(id+"F1.opExtrude","CAP_FACE",FACE,{"disambiguationData":[OSD([sQuery(id+"F0.wireOp",EDGE,"E2.0.0.27"),sQuery(id+"F0.wireOp",EDGE,"E2.3.0.27"),sQuery(id+"F0.wireOp",EDGE,"E2.6.0.27"),sQuery(id+"F0.wireOp",EDGE,"E2.9.0.27")])],"isStart":true});
            var Q61;
            Q61=makeQuery(id+"F1.opExtrude","CAP_FACE",FACE,{"disambiguationData":[OSD([sQuery(id+"F0.wireOp",EDGE,"E2.0.0.28"),sQuery(id+"F0.wireOp",EDGE,"E2.3.0.28"),sQuery(id+"F0.wireOp",EDGE,"E2.6.0.28"),sQuery(id+"F0.wireOp",EDGE,"E2.9.0.28")])],"isStart":true});
            var Q62;
            Q62=makeQuery(id+"F1.opExtrude","CAP_FACE",FACE,{"disambiguationData":[OSD([sQuery(id+"F0.wireOp",EDGE,"E2.0.0.29"),sQuery(id+"F0.wireOp",EDGE,"E2.3.0.29"),sQuery(id+"F0.wireOp",EDGE,"E2.6.0.29"),sQuery(id+"F0.wireOp",EDGE,"E2.9.0.29")])],"isStart":true});
            var Q63;
            Q63=makeQuery(id+"F1.opExtrude","CAP_FACE",FACE,{"disambiguationData":[OSD([sQuery(id+"F0.wireOp",EDGE,"E3.0.0.30"),sQuery(id+"F0.wireOp",EDGE,"E3.3.0.30"),sQuery(id+"F0.wireOp",EDGE,"E3.6.0.30"),sQuery(id+"F0.wireOp",EDGE,"E3.9.0.30")])],"isStart":true});
            var Q64;
            Q64=makeQuery(id+"F1.opExtrude","CAP_FACE",FACE,{"disambiguationData":[OSD([sQuery(id+"F0.wireOp",EDGE,"E3.0.0.30"),sQuery(id+"F0.wireOp",EDGE,"E3.3.0.30"),sQuery(id+"F0.wireOp",EDGE,"E3.6.0.30"),sQuery(id+"F0.wireOp",EDGE,"E3.9.0.30")])],"isStart":true});
            var Q65;
            Q65=makeQuery(id+"F1.opExtrude","CAP_FACE",FACE,{"disambiguationData":[OSD([sQuery(id+"F0.wireOp",EDGE,"E3.0.0.31"),sQuery(id+"F0.wireOp",EDGE,"E3.3.0.31"),sQuery(id+"F0.wireOp",EDGE,"E3.6.0.31"),sQuery(id+"F0.wireOp",EDGE,"E3.9.0.31")])],"isStart":true});
            var Q66;
            Q66=makeQuery(id+"F1.opExtrude","CAP_FACE",FACE,{"disambiguationData":[OSD([sQuery(id+"F0.wireOp",EDGE,"E3.0.0.32"),sQuery(id+"F0.wireOp",EDGE,"E3.3.0.32"),sQuery(id+"F0.wireOp",EDGE,"E3.6.0.32"),sQuery(id+"F0.wireOp",EDGE,"E3.9.0.32")])],"isStart":true});
            var Q67;
            Q67=makeQuery(id+"F1.opExtrude","CAP_FACE",FACE,{"disambiguationData":[OSD([sQuery(id+"F0.wireOp",EDGE,"E3.0.0.33"),sQuery(id+"F0.wireOp",EDGE,"E3.3.0.33"),sQuery(id+"F0.wireOp",EDGE,"E3.6.0.33"),sQuery(id+"F0.wireOp",EDGE,"E3.9.0.33")])],"isStart":true});
            var Q68;
            Q68=makeQuery(id+"F1.opExtrude","CAP_FACE",FACE,{"disambiguationData":[OSD([sQuery(id+"F0.wireOp",EDGE,"E3.0.0.34"),sQuery(id+"F0.wireOp",EDGE,"E3.3.0.34"),sQuery(id+"F0.wireOp",EDGE,"E3.6.0.34"),sQuery(id+"F0.wireOp",EDGE,"E3.9.0.34")])],"isStart":true});
            var Q69;
            Q69=makeQuery(id+"F1.opExtrude","CAP_FACE",FACE,{"disambiguationData":[OSD([sQuery(id+"F0.wireOp",EDGE,"E3.0.0.35"),sQuery(id+"F0.wireOp",EDGE,"E3.3.0.35"),sQuery(id+"F0.wireOp",EDGE,"E3.6.0.35"),sQuery(id+"F0.wireOp",EDGE,"E3.9.0.35")])],"isStart":true});
            var Q70;
            Q70=makeQuery(id+"F1.opExtrude","CAP_FACE",FACE,{"disambiguationData":[OSD([sQuery(id+"F0.wireOp",EDGE,"E3.0.0.36"),sQuery(id+"F0.wireOp",EDGE,"E3.3.0.36"),sQuery(id+"F0.wireOp",EDGE,"E3.6.0.36"),sQuery(id+"F0.wireOp",EDGE,"E3.9.0.36")])],"isStart":true});
            var Q71;
            Q71=makeQuery(id+"F1.opExtrude","SWEPT_FACE",FACE,{"disambiguationData":[OSD([sQuery(id+"F0.wireOp",EDGE,"E3.9.0.36")])]});
            var Q72;
            Q72=makeQuery(id+"F1.opExtrude","SWEPT_FACE",FACE,{"disambiguationData":[OSD([sQuery(id+"F0.wireOp",EDGE,"E3.9.0.35")])]});
            var Q73;
            Q73=makeQuery(id+"F1.opExtrude","SWEPT_FACE",FACE,{"disambiguationData":[OSD([sQuery(id+"F0.wireOp",EDGE,"E3.9.0.34")])]});
            var Q74;
            Q74=makeQuery(id+"F1.opExtrude","SWEPT_FACE",FACE,{"disambiguationData":[OSD([sQuery(id+"F0.wireOp",EDGE,"E3.9.0.33")])]});
            var Q75;
            Q75=makeQuery(id+"F1.opExtrude","SWEPT_FACE",FACE,{"disambiguationData":[OSD([sQuery(id+"F0.wireOp",EDGE,"E3.9.0.32")])]});
            var Q76;
            Q76=makeQuery(id+"F1.opExtrude","SWEPT_FACE",FACE,{"disambiguationData":[OSD([sQuery(id+"F0.wireOp",EDGE,"E3.9.0.31")])]});
            var Q77;
            Q77=makeQuery(id+"F1.opExtrude","SWEPT_FACE",FACE,{"disambiguationData":[OSD([sQuery(id+"F0.wireOp",EDGE,"E3.9.0.30")])]});
            var Q78;
            Q78=makeQuery(id+"F1.opExtrude","SWEPT_FACE",FACE,{"disambiguationData":[OSD([sQuery(id+"F0.wireOp",EDGE,"E2.9.0.29")])]});
            var Q79;
            Q79=makeQuery(id+"F1.opExtrude","SWEPT_FACE",FACE,{"disambiguationData":[OSD([sQuery(id+"F0.wireOp",EDGE,"E2.9.0.28")])]});
            var Q80;
            Q80=makeQuery(id+"F1.opExtrude","SWEPT_FACE",FACE,{"disambiguationData":[OSD([sQuery(id+"F0.wireOp",EDGE,"E2.9.0.27")])]});
            var Q81;
            Q81=makeQuery(id+"F1.opExtrude","SWEPT_FACE",FACE,{"disambiguationData":[OSD([sQuery(id+"F0.wireOp",EDGE,"E2.9.0.26")])]});
            var Q82;
            Q82=makeQuery(id+"F1.opExtrude","SWEPT_FACE",FACE,{"disambiguationData":[OSD([sQuery(id+"F0.wireOp",EDGE,"E2.9.0.25")])]});
            var Q83;
            Q83=makeQuery(id+"F1.opExtrude","SWEPT_FACE",FACE,{"disambiguationData":[OSD([sQuery(id+"F0.wireOp",EDGE,"E2.9.0.24")])]});
            var Q84;
            Q84=makeQuery(id+"F1.opExtrude","SWEPT_FACE",FACE,{"disambiguationData":[OSD([sQuery(id+"F0.wireOp",EDGE,"E2.9.0.23")])]});
            var Q85;
            Q85=makeQuery(id+"F1.opExtrude","SWEPT_FACE",FACE,{"disambiguationData":[OSD([sQuery(id+"F0.wireOp",EDGE,"E2.9.0.22")])]});
            var Q86;
            Q86=makeQuery(id+"F1.opExtrude","SWEPT_FACE",FACE,{"disambiguationData":[OSD([sQuery(id+"F0.wireOp",EDGE,"E2.9.0.21")])]});
            var Q87;
            Q87=makeQuery(id+"F1.opExtrude","SWEPT_FACE",FACE,{"disambiguationData":[OSD([sQuery(id+"F0.wireOp",EDGE,"E2.9.0.20")])]});
            var Q88;
            Q88=makeQuery(id+"F1.opExtrude","SWEPT_FACE",FACE,{"disambiguationData":[OSD([sQuery(id+"F0.wireOp",EDGE,"E1.0.19.3")])]});
            var Q89;
            Q89=makeQuery(id+"F1.opExtrude","SWEPT_FACE",FACE,{"disambiguationData":[OSD([sQuery(id+"F0.wireOp",EDGE,"E1.0.18.3")])]});
            var Q90;
            Q90=makeQuery(id+"F1.opExtrude","CAP_FACE",FACE,{"disambiguationData":[OSD([sQuery(id+"F0.wireOp",EDGE,"E2.0.0.20"),sQuery(id+"F0.wireOp",EDGE,"E2.3.0.20"),sQuery(id+"F0.wireOp",EDGE,"E2.6.0.20"),sQuery(id+"F0.wireOp",EDGE,"E2.9.0.20")])],"isStart":true});
            var Q91;
            Q91=makeQuery(id+"F1.opExtrude","CAP_FACE",FACE,{"disambiguationData":[OSD([sQuery(id+"F0.wireOp",EDGE,"E1.0.19.0"),sQuery(id+"F0.wireOp",EDGE,"E1.0.19.1"),sQuery(id+"F0.wireOp",EDGE,"E1.0.19.2"),sQuery(id+"F0.wireOp",EDGE,"E1.0.19.3")])],"isStart":true});
            var Q92;
            Q92=makeQuery(id+"F1.opExtrude","SWEPT_FACE",FACE,{"disambiguationData":[OSD([sQuery(id+"F0.wireOp",EDGE,"E1.0.17.3")])]});
            var Q93;
            Q93=makeQuery(id+"F1.opExtrude","SWEPT_FACE",FACE,{"disambiguationData":[OSD([sQuery(id+"F0.wireOp",EDGE,"E1.0.16.3")])]});
            var Q94;
            Q94=makeQuery(id+"F1.opExtrude","SWEPT_FACE",FACE,{"disambiguationData":[OSD([sQuery(id+"F0.wireOp",EDGE,"E1.0.14.3")])]});
            var Q95;
            Q95=makeQuery(id+"F1.opExtrude","SWEPT_FACE",FACE,{"disambiguationData":[OSD([sQuery(id+"F0.wireOp",EDGE,"E1.0.15.3")])]});
            var Q96;
            Q96=makeQuery(id+"F1.opExtrude","SWEPT_FACE",FACE,{"disambiguationData":[OSD([sQuery(id+"F0.wireOp",EDGE,"E1.0.13.3")])]});
            var Q97;
            Q97=makeQuery(id+"F1.opExtrude","SWEPT_FACE",FACE,{"disambiguationData":[OSD([sQuery(id+"F0.wireOp",EDGE,"E1.0.12.3")])]});
            var Q98;
            Q98=makeQuery(id+"F1.opExtrude","SWEPT_FACE",FACE,{"disambiguationData":[OSD([sQuery(id+"F0.wireOp",EDGE,"E1.0.11.3")])]});
            var Q99;
            Q99=makeQuery(id+"F1.opExtrude","CAP_FACE",FACE,{"disambiguationData":[OSD([sQuery(id+"F0.wireOp",EDGE,"E1.0.16.0"),sQuery(id+"F0.wireOp",EDGE,"E1.0.16.1"),sQuery(id+"F0.wireOp",EDGE,"E1.0.16.2"),sQuery(id+"F0.wireOp",EDGE,"E1.0.16.3")])],"isStart":false});
            var Q100;
            Q100=makeQuery(id+"F1.opExtrude","SWEPT_FACE",FACE,{"disambiguationData":[OSD([sQuery(id+"F0.wireOp",EDGE,"E3.6.0.36")])]});
            var Q101;
            Q101=makeQuery(id+"F1.opExtrude","SWEPT_FACE",FACE,{"disambiguationData":[OSD([sQuery(id+"F0.wireOp",EDGE,"E3.6.0.35")])]});
            var Q102;
            Q102=makeQuery(id+"F1.opExtrude","SWEPT_FACE",FACE,{"disambiguationData":[OSD([sQuery(id+"F0.wireOp",EDGE,"E3.6.0.34")])]});
            var Q103;
            Q103=makeQuery(id+"F1.opExtrude","SWEPT_FACE",FACE,{"disambiguationData":[OSD([sQuery(id+"F0.wireOp",EDGE,"E3.6.0.33")])]});
            var Q104;
            Q104=makeQuery(id+"F1.opExtrude","SWEPT_FACE",FACE,{"disambiguationData":[OSD([sQuery(id+"F0.wireOp",EDGE,"E3.6.0.32")])]});
            var Q105;
            Q105=makeQuery(id+"F1.opExtrude","SWEPT_FACE",FACE,{"disambiguationData":[OSD([sQuery(id+"F0.wireOp",EDGE,"E3.6.0.31")])]});
            var Q106;
            Q106=makeQuery(id+"F1.opExtrude","SWEPT_FACE",FACE,{"disambiguationData":[OSD([sQuery(id+"F0.wireOp",EDGE,"E3.6.0.30")])]});
            var Q107;
            Q107=makeQuery(id+"F1.opExtrude","SWEPT_FACE",FACE,{"disambiguationData":[OSD([sQuery(id+"F0.wireOp",EDGE,"E2.6.0.29")])]});
            var Q108;
            Q108=makeQuery(id+"F1.opExtrude","SWEPT_FACE",FACE,{"disambiguationData":[OSD([sQuery(id+"F0.wireOp",EDGE,"E2.6.0.28")])]});
            var Q109;
            Q109=makeQuery(id+"F1.opExtrude","SWEPT_FACE",FACE,{"disambiguationData":[OSD([sQuery(id+"F0.wireOp",EDGE,"E2.6.0.27")])]});
            var Q110;
            Q110=makeQuery(id+"F1.opExtrude","SWEPT_FACE",FACE,{"disambiguationData":[OSD([sQuery(id+"F0.wireOp",EDGE,"E2.6.0.26")])]});
            var Q111;
            Q111=makeQuery(id+"F1.opExtrude","SWEPT_FACE",FACE,{"disambiguationData":[OSD([sQuery(id+"F0.wireOp",EDGE,"E2.6.0.25")])]});
            var Q112;
            Q112=makeQuery(id+"F1.opExtrude","SWEPT_FACE",FACE,{"disambiguationData":[OSD([sQuery(id+"F0.wireOp",EDGE,"E2.6.0.24")])]});
            var Q113;
            Q113=makeQuery(id+"F1.opExtrude","SWEPT_FACE",FACE,{"disambiguationData":[OSD([sQuery(id+"F0.wireOp",EDGE,"E2.6.0.23")])]});
            var Q114;
            Q114=makeQuery(id+"F1.opExtrude","SWEPT_FACE",FACE,{"disambiguationData":[OSD([sQuery(id+"F0.wireOp",EDGE,"E2.6.0.22")])]});
            var Q115;
            Q115=makeQuery(id+"F1.opExtrude","SWEPT_FACE",FACE,{"disambiguationData":[OSD([sQuery(id+"F0.wireOp",EDGE,"E2.6.0.21")])]});
            var Q116;
            Q116=makeQuery(id+"F1.opExtrude","SWEPT_FACE",FACE,{"disambiguationData":[OSD([sQuery(id+"F0.wireOp",EDGE,"E2.6.0.20")])]});
            var Q117;
            Q117=makeQuery(id+"F1.opExtrude","SWEPT_FACE",FACE,{"disambiguationData":[OSD([sQuery(id+"F0.wireOp",EDGE,"E1.0.19.2")])]});
            var Q118;
            Q118=makeQuery(id+"F1.opExtrude","SWEPT_FACE",FACE,{"disambiguationData":[OSD([sQuery(id+"F0.wireOp",EDGE,"E1.0.18.2")])]});
            var Q119;
            Q119=makeQuery(id+"F1.opExtrude","SWEPT_FACE",FACE,{"disambiguationData":[OSD([sQuery(id+"F0.wireOp",EDGE,"E1.0.17.2")])]});
            var Q120;
            Q120=makeQuery(id+"F1.opExtrude","SWEPT_FACE",FACE,{"disambiguationData":[OSD([sQuery(id+"F0.wireOp",EDGE,"E1.0.16.2")])]});
            var Q121;
            Q121=makeQuery(id+"F1.opExtrude","SWEPT_FACE",FACE,{"disambiguationData":[OSD([sQuery(id+"F0.wireOp",EDGE,"E1.0.15.2")])]});
            var Q122;
            Q122=makeQuery(id+"F1.opExtrude","SWEPT_FACE",FACE,{"disambiguationData":[OSD([sQuery(id+"F0.wireOp",EDGE,"E1.0.14.2")])]});
            var Q123;
            Q123=makeQuery(id+"F1.opExtrude","SWEPT_FACE",FACE,{"disambiguationData":[OSD([sQuery(id+"F0.wireOp",EDGE,"E1.0.13.2")])]});
            var Q124;
            Q124=makeQuery(id+"F1.opExtrude","SWEPT_FACE",FACE,{"disambiguationData":[OSD([sQuery(id+"F0.wireOp",EDGE,"E1.0.12.2")])]});
            var Q125;
            Q125=makeQuery(id+"F1.opExtrude","SWEPT_FACE",FACE,{"disambiguationData":[OSD([sQuery(id+"F0.wireOp",EDGE,"E1.0.11.2")])]});
            var Q126;
            Q126=makeQuery(id+"F1.opExtrude","SWEPT_FACE",FACE,{"disambiguationData":[OSD([sQuery(id+"F0.wireOp",EDGE,"E1.0.10.2")])]});
            var Q127;
            Q127=makeQuery(id+"F1.opExtrude","SWEPT_FACE",FACE,{"disambiguationData":[OSD([sQuery(id+"F0.wireOp",EDGE,"E1.0.9.2")])]});
            var Q128;
            Q128=makeQuery(id+"F1.opExtrude","SWEPT_FACE",FACE,{"disambiguationData":[OSD([sQuery(id+"F0.wireOp",EDGE,"E1.0.8.2")])]});
            var Q129;
            Q129=makeQuery(id+"F1.opExtrude","SWEPT_FACE",FACE,{"disambiguationData":[OSD([sQuery(id+"F0.wireOp",EDGE,"E1.0.7.2")])]});
            var Q130;
            Q130=makeQuery(id+"F1.opExtrude","SWEPT_FACE",FACE,{"disambiguationData":[OSD([sQuery(id+"F0.wireOp",EDGE,"E1.0.6.2")])]});
            var Q131;
            Q131=makeQuery(id+"F1.opExtrude","SWEPT_FACE",FACE,{"disambiguationData":[OSD([sQuery(id+"F0.wireOp",EDGE,"E1.0.5.2")])]});
            var Q132;
            Q132=makeQuery(id+"F1.opExtrude","SWEPT_FACE",FACE,{"disambiguationData":[OSD([sQuery(id+"F0.wireOp",EDGE,"E1.0.4.2")])]});
            var Q133;
            Q133=makeQuery(id+"F1.opExtrude","SWEPT_FACE",FACE,{"disambiguationData":[OSD([sQuery(id+"F0.wireOp",EDGE,"E1.0.3.2")])]});
            var Q134;
            Q134=makeQuery(id+"F1.opExtrude","SWEPT_FACE",FACE,{"disambiguationData":[OSD([sQuery(id+"F0.wireOp",EDGE,"E1.0.2.2")])]});
            var Q135;
            Q135=makeQuery(id+"F1.opExtrude","SWEPT_FACE",FACE,{"disambiguationData":[OSD([sQuery(id+"F0.wireOp",EDGE,"E1.0.1.2")])]});
            var Q136;
            Q136=makeQuery(id+"F1.opExtrude","SWEPT_FACE",FACE,{"disambiguationData":[OSD([sQuery(id+"F0.wireOp",EDGE,"E0.left")])]});
            var Q137;
            Q137=makeQuery(id+"F1.opExtrude","CAP_FACE",FACE,{"disambiguationData":[OSD([sQuery(id+"F0.wireOp",EDGE,"E0.bottom"),sQuery(id+"F0.wireOp",EDGE,"E0.top"),sQuery(id+"F0.wireOp",EDGE,"E0.left"),sQuery(id+"F0.wireOp",EDGE,"E0.right")])],"isStart":true});
            var Q138;
            Q138=makeQuery(id+"F1.opExtrude","SWEPT_FACE",FACE,{"disambiguationData":[OSD([sQuery(id+"F0.wireOp",EDGE,"E0.right")])]});
            var Q139;
            Q139=makeQuery(id+"F1.opExtrude","SWEPT_FACE",FACE,{"disambiguationData":[OSD([sQuery(id+"F0.wireOp",EDGE,"E1.0.1.3")])]});
            var Q140;
            Q140=makeQuery(id+"F1.opExtrude","SWEPT_FACE",FACE,{"disambiguationData":[OSD([sQuery(id+"F0.wireOp",EDGE,"E1.0.2.3")])]});
            var Q141;
            Q141=makeQuery(id+"F1.opExtrude","SWEPT_FACE",FACE,{"disambiguationData":[OSD([sQuery(id+"F0.wireOp",EDGE,"E1.0.3.3")])]});
            var Q142;
            Q142=makeQuery(id+"F1.opExtrude","SWEPT_FACE",FACE,{"disambiguationData":[OSD([sQuery(id+"F0.wireOp",EDGE,"E1.0.4.3")])]});
            var Q143;
            Q143=makeQuery(id+"F1.opExtrude","SWEPT_FACE",FACE,{"disambiguationData":[OSD([sQuery(id+"F0.wireOp",EDGE,"E1.0.5.3")])]});
            var Q144;
            Q144=makeQuery(id+"F1.opExtrude","SWEPT_FACE",FACE,{"disambiguationData":[OSD([sQuery(id+"F0.wireOp",EDGE,"E1.0.6.3")])]});
            var Q145;
            Q145=makeQuery(id+"F1.opExtrude","SWEPT_FACE",FACE,{"disambiguationData":[OSD([sQuery(id+"F0.wireOp",EDGE,"E1.0.7.3")])]});
            var Q146;
            Q146=makeQuery(id+"F1.opExtrude","SWEPT_FACE",FACE,{"disambiguationData":[OSD([sQuery(id+"F0.wireOp",EDGE,"E1.0.8.3")])]});
            var Q147;
            Q147=makeQuery(id+"F1.opExtrude","SWEPT_FACE",FACE,{"disambiguationData":[OSD([sQuery(id+"F0.wireOp",EDGE,"E1.0.9.3")])]});
            var Q148;
            Q148=makeQuery(id+"F1.opExtrude","SWEPT_FACE",FACE,{"disambiguationData":[OSD([sQuery(id+"F0.wireOp",EDGE,"E1.0.10.3")])]});
            fillet(context, id + "F2", {"entities" : qUnion([Q0, Q1, Q2, Q3, Q4, Q5, Q6, Q7, Q8, Q9, Q10, Q11, Q12, Q13, Q14, Q15, Q16, Q17, Q18, Q19, Q20, Q21, Q22, Q23, Q24, Q25, Q26, Q27, Q28, Q29, Q30, Q31, Q32, Q33, Q34, Q35, Q36, Q37, Q38, Q39, Q40, Q41, Q42, Q43, Q44, Q45, Q46, Q47, Q48, Q49, Q50, Q51, Q52, Q53, Q54, Q55, Q56, Q57, Q58, Q59, Q60, Q61, Q62, Q63, Q64, Q65, Q66, Q67, Q68, Q69, Q70, Q71, Q72, Q73, Q74, Q75, Q76, Q77, Q78, Q79, Q80, Q81, Q82, Q83, Q84, Q85, Q86, Q87, Q88, Q89, Q90, Q91, Q92, Q93, Q94, Q95, Q96, Q97, Q98, Q99, Q100, Q101, Q102, Q103, Q104, Q105, Q106, Q107, Q108, Q109, Q110, Q111, Q112, Q113, Q114, Q115, Q116, Q117, Q118, Q119, Q120, Q121, Q122, Q123, Q124, Q125, Q126, Q127, Q128, Q129, Q130, Q131, Q132, Q133, Q134, Q135, Q136, Q137, Q138, Q139, Q140, Q141, Q142, Q143, Q144, Q145, Q146, Q147, Q148]), "radius" : 0.25 * mm, "tangentPropagation" : true, "allowEdgeOverflow" : false});
        }
        {
            var Q0;
            Q0=qCreatedBy(makeId("Front.planeOp"),FACE);
            var sketch = newSketch(context, id + "F3", { "sketchPlane" : qUnion([Q0])});
            skLineSegment(sketch, "E4", {"start": v(-10.06, 2.7) * mm, "end": v(-7.98, 2.7) * mm});
            skLineSegment(sketch, "E5", {"start": v(-9.61, 4.47) * mm, "end": v(-8.42, 4.47) * mm});
            skLineSegment(sketch, "E6", {"start": v(-8.42, 4.47) * mm, "end": v(-8.42, 4.02) * mm});
            skLineSegment(sketch, "E7", {"start": v(-8.42, 4.02) * mm, "end": v(-8.56, 4.02) * mm});
            skLineSegment(sketch, "E8", {"start": v(-8.56, 4.02) * mm, "end": v(-8.56, 3.18) * mm});
            skLineSegment(sketch, "E9", {"start": v(-8.56, 3.18) * mm, "end": v(-7.98, 3) * mm});
            skLineSegment(sketch, "E10", {"start": v(-7.98, 3) * mm, "end": v(-7.98, 2.7) * mm});
            skPoint(sketch, "E11.end.orphan", {"position": v(-9.02, 4.47) * mm});
            skPoint(sketch, "E11.start.orphan", {"position": v(-9.02, 2.7) * mm});
            skLineSegment(sketch, "E12.MirrorCS", {"start": v(-9.61, 4.47) * mm, "end": v(-9.61, 4.02) * mm});
            skLineSegment(sketch, "E13.MirrorCS", {"start": v(-9.61, 4.02) * mm, "end": v(-9.47, 4.02) * mm});
            skLineSegment(sketch, "E14.MirrorCS", {"start": v(-9.47, 4.02) * mm, "end": v(-9.47, 3.18) * mm});
            skLineSegment(sketch, "E15.MirrorCS", {"start": v(-9.47, 3.18) * mm, "end": v(-10.06, 3) * mm});
            skLineSegment(sketch, "E16.MirrorCS", {"start": v(-10.06, 3) * mm, "end": v(-10.06, 2.7) * mm});
            skLineSegment(sketch, "E17.MirrorCS", {"start": v(8.42, 4.47) * mm, "end": v(8.42, 4.02) * mm});
            skLineSegment(sketch, "E18.MirrorCS", {"start": v(9.61, 4.47) * mm, "end": v(9.61, 4.02) * mm});
            skLineSegment(sketch, "E19.MirrorCS", {"start": v(8.42, 4.02) * mm, "end": v(8.56, 4.02) * mm});
            skLineSegment(sketch, "E20.MirrorCS", {"start": v(9.61, 4.02) * mm, "end": v(9.47, 4.02) * mm});
            skLineSegment(sketch, "E21.MirrorCS", {"start": v(9.47, 3.18) * mm, "end": v(10.06, 3) * mm});
            skLineSegment(sketch, "E22.MirrorCS", {"start": v(7.98, 3) * mm, "end": v(7.98, 2.7) * mm});
            skLineSegment(sketch, "E23.MirrorCS", {"start": v(10.06, 3) * mm, "end": v(10.06, 2.7) * mm});
            skLineSegment(sketch, "E24.MirrorCS", {"start": v(9.61, 4.47) * mm, "end": v(8.42, 4.47) * mm});
            skLineSegment(sketch, "E25.MirrorCS", {"start": v(8.56, 4.02) * mm, "end": v(8.56, 3.18) * mm});
            skLineSegment(sketch, "E26.MirrorCS", {"start": v(9.47, 4.02) * mm, "end": v(9.47, 3.18) * mm});
            skPoint(sketch, "E27.MirrorP", {"position": v(9.02, 4.47) * mm});
            skLineSegment(sketch, "E28.MirrorCS", {"start": v(8.56, 3.18) * mm, "end": v(7.98, 3) * mm});
            skLineSegment(sketch, "E29.MirrorCS", {"start": v(10.06, 2.7) * mm, "end": v(7.98, 2.7) * mm});
            skPoint(sketch, "E30.MirrorP", {"position": v(9.02, 2.7) * mm});
            skSolve(sketch);
        }
        {
            var Q0;
            Q0 = qSketchRegion(id + "F3", true);
            extrude(context, id + "F4", {"entities" : qUnion([Q0]), "operationType" : NewBodyOperationType.ADD, "oppositeDirection" : true, "depth" : 220.98 * mm, "hasSecondDirection" : true, "secondDirectionOppositeDirection" : false, "secondDirectionDepth" : 7.62 * mm});
        }
        {
            var Q0;
            Q0=makeQuery(id+"F4.opExtrude","SWEPT_FACE",FACE,{"disambiguationData":[OSD([sQuery(id+"F3.wireOp",EDGE,"E9")])]});
            var sketch = newSketch(context, id + "F5", { "sketchPlane" : qUnion([Q0])});
            skEllipse(sketch, "E31", {"center": v(-8.51, -1.35) * mm, "majorRadius": 0.28 * mm, "minorRadius": 0.2 * mm, "majorAxis": v(1, 0)});
            skEllipse(sketch, "E32.1.0.0", {"center": v(-8.51, 4.83) * mm, "majorRadius": 0.28 * mm, "minorRadius": 0.2 * mm, "majorAxis": v(1, 0)});
            skEllipse(sketch, "E32.2.0.0", {"center": v(-8.51, 11) * mm, "majorRadius": 0.28 * mm, "minorRadius": 0.2 * mm, "majorAxis": v(1, 0)});
            skEllipse(sketch, "E32.3.0.0", {"center": v(-8.51, 17.17) * mm, "majorRadius": 0.28 * mm, "minorRadius": 0.2 * mm, "majorAxis": v(1, 0)});
            skEllipse(sketch, "E32.4.0.0", {"center": v(-8.51, 23.34) * mm, "majorRadius": 0.28 * mm, "minorRadius": 0.2 * mm, "majorAxis": v(1, 0)});
            skEllipse(sketch, "E32.5.0.0", {"center": v(-8.51, 29.51) * mm, "majorRadius": 0.28 * mm, "minorRadius": 0.2 * mm, "majorAxis": v(1, 0)});
            skEllipse(sketch, "E32.6.0.0", {"center": v(-8.51, 35.69) * mm, "majorRadius": 0.28 * mm, "minorRadius": 0.2 * mm, "majorAxis": v(1, 0)});
            skEllipse(sketch, "E32.7.0.0", {"center": v(-8.51, 41.86) * mm, "majorRadius": 0.28 * mm, "minorRadius": 0.2 * mm, "majorAxis": v(1, 0)});
            skEllipse(sketch, "E32.8.0.0", {"center": v(-8.51, 48.03) * mm, "majorRadius": 0.28 * mm, "minorRadius": 0.2 * mm, "majorAxis": v(1, 0)});
            skEllipse(sketch, "E32.9.0.0", {"center": v(-8.51, 54.2) * mm, "majorRadius": 0.28 * mm, "minorRadius": 0.2 * mm, "majorAxis": v(1, 0)});
            skEllipse(sketch, "E32.10.0.0", {"center": v(-8.51, 60.38) * mm, "majorRadius": 0.28 * mm, "minorRadius": 0.2 * mm, "majorAxis": v(1, 0)});
            skEllipse(sketch, "E32.11.0.0", {"center": v(-8.51, 66.55) * mm, "majorRadius": 0.28 * mm, "minorRadius": 0.2 * mm, "majorAxis": v(1, 0)});
            skEllipse(sketch, "E32.12.0.0", {"center": v(-8.51, 72.72) * mm, "majorRadius": 0.28 * mm, "minorRadius": 0.2 * mm, "majorAxis": v(1, 0)});
            skEllipse(sketch, "E32.13.0.0", {"center": v(-8.51, 78.9) * mm, "majorRadius": 0.28 * mm, "minorRadius": 0.2 * mm, "majorAxis": v(1, 0)});
            skEllipse(sketch, "E32.14.0.0", {"center": v(-8.51, 85.06) * mm, "majorRadius": 0.28 * mm, "minorRadius": 0.2 * mm, "majorAxis": v(1, 0)});
            skEllipse(sketch, "E32.15.0.0", {"center": v(-8.51, 91.24) * mm, "majorRadius": 0.28 * mm, "minorRadius": 0.2 * mm, "majorAxis": v(1, 0)});
            skEllipse(sketch, "E32.16.0.0", {"center": v(-8.51, 97.4) * mm, "majorRadius": 0.28 * mm, "minorRadius": 0.2 * mm, "majorAxis": v(1, 0)});
            skEllipse(sketch, "E32.17.0.0", {"center": v(-8.51, 103.58) * mm, "majorRadius": 0.28 * mm, "minorRadius": 0.2 * mm, "majorAxis": v(1, 0)});
            skEllipse(sketch, "E32.18.0.0", {"center": v(-8.51, 109.75) * mm, "majorRadius": 0.28 * mm, "minorRadius": 0.2 * mm, "majorAxis": v(1, 0)});
            skEllipse(sketch, "E32.19.0.0", {"center": v(-8.51, 115.93) * mm, "majorRadius": 0.28 * mm, "minorRadius": 0.2 * mm, "majorAxis": v(1, 0)});
            skEllipse(sketch, "E32.20.0.0", {"center": v(-8.51, 122.1) * mm, "majorRadius": 0.28 * mm, "minorRadius": 0.2 * mm, "majorAxis": v(1, 0)});
            skEllipse(sketch, "E32.21.0.0", {"center": v(-8.51, 128.27) * mm, "majorRadius": 0.28 * mm, "minorRadius": 0.2 * mm, "majorAxis": v(1, 0)});
            skEllipse(sketch, "E32.22.0.0", {"center": v(-8.51, 134.44) * mm, "majorRadius": 0.28 * mm, "minorRadius": 0.2 * mm, "majorAxis": v(1, 0)});
            skEllipse(sketch, "E32.23.0.0", {"center": v(-8.51, 140.61) * mm, "majorRadius": 0.28 * mm, "minorRadius": 0.2 * mm, "majorAxis": v(1, 0)});
            skEllipse(sketch, "E32.24.0.0", {"center": v(-8.51, 146.79) * mm, "majorRadius": 0.28 * mm, "minorRadius": 0.2 * mm, "majorAxis": v(1, 0)});
            skEllipse(sketch, "E32.25.0.0", {"center": v(-8.51, 152.96) * mm, "majorRadius": 0.28 * mm, "minorRadius": 0.2 * mm, "majorAxis": v(1, 0)});
            skEllipse(sketch, "E32.26.0.0", {"center": v(-8.51, 159.13) * mm, "majorRadius": 0.28 * mm, "minorRadius": 0.2 * mm, "majorAxis": v(1, 0)});
            skEllipse(sketch, "E32.27.0.0", {"center": v(-8.51, 165.3) * mm, "majorRadius": 0.28 * mm, "minorRadius": 0.2 * mm, "majorAxis": v(1, 0)});
            skLineSegment(sketch, "E32.direction1", {"start": v(-8.51, -1.35) * mm, "end": v(-8.51, 4.83) * mm, "construction": true});
            skEllipse(sketch, "E33.0.28.0", {"center": v(-8.51, 171.48) * mm, "majorRadius": 0.28 * mm, "minorRadius": 0.2 * mm, "majorAxis": v(1, 0)});
            skEllipse(sketch, "E33.0.29.0", {"center": v(-8.51, 177.65) * mm, "majorRadius": 0.28 * mm, "minorRadius": 0.2 * mm, "majorAxis": v(1, 0)});
            skEllipse(sketch, "E33.0.30.0", {"center": v(-8.51, 183.82) * mm, "majorRadius": 0.28 * mm, "minorRadius": 0.2 * mm, "majorAxis": v(1, 0)});
            skEllipse(sketch, "E33.0.31.0", {"center": v(-8.51, 190) * mm, "majorRadius": 0.28 * mm, "minorRadius": 0.2 * mm, "majorAxis": v(1, 0)});
            skEllipse(sketch, "E33.0.32.0", {"center": v(-8.51, 196.16) * mm, "majorRadius": 0.28 * mm, "minorRadius": 0.2 * mm, "majorAxis": v(1, 0)});
            skEllipse(sketch, "E33.0.33.0", {"center": v(-8.51, 202.34) * mm, "majorRadius": 0.28 * mm, "minorRadius": 0.2 * mm, "majorAxis": v(1, 0)});
            skEllipse(sketch, "E33.0.34.0", {"center": v(-8.51, 208.5) * mm, "majorRadius": 0.28 * mm, "minorRadius": 0.2 * mm, "majorAxis": v(1, 0)});
            skEllipse(sketch, "E33.0.35.0", {"center": v(-8.51, 214.68) * mm, "majorRadius": 0.28 * mm, "minorRadius": 0.2 * mm, "majorAxis": v(1, 0)});
            skEllipse(sketch, "E33.0.36.0", {"center": v(-8.51, 220.85) * mm, "majorRadius": 0.28 * mm, "minorRadius": 0.2 * mm, "majorAxis": v(1, 0)});
            skSolve(sketch);
        }
        {
            var Q0;
            Q0 = qSketchRegion(id + "F5", true);
            extrude(context, id + "F6", {"entities" : qUnion([Q0]), "operationType" : NewBodyOperationType.ADD, "depth" : 0.25 * mm, "hasSecondDirection" : true, "secondDirectionOppositeDirection" : true, "secondDirectionDepth" : 0.5 * mm});
        }
        {
            var Q0;
            Q0=makeQuery(id+"F4.opExtrude","SWEPT_FACE",FACE,{"disambiguationData":[OSD([sQuery(id+"F3.wireOp",EDGE,"E28.MirrorCS")])]});
            var sketch = newSketch(context, id + "F7", { "sketchPlane" : qUnion([Q0])});
            skEllipse(sketch, "E34", {"center": v(8.51, -1.35) * mm, "majorRadius": 0.28 * mm, "minorRadius": 0.2 * mm, "majorAxis": v(-1, 0)});
            skEllipse(sketch, "E35.1.0.0", {"center": v(8.51, 4.83) * mm, "majorRadius": 0.28 * mm, "minorRadius": 0.2 * mm, "majorAxis": v(-1, 0)});
            skEllipse(sketch, "E35.2.0.0", {"center": v(8.51, 11) * mm, "majorRadius": 0.28 * mm, "minorRadius": 0.2 * mm, "majorAxis": v(-1, 0)});
            skEllipse(sketch, "E35.3.0.0", {"center": v(8.51, 17.17) * mm, "majorRadius": 0.28 * mm, "minorRadius": 0.2 * mm, "majorAxis": v(-1, 0)});
            skEllipse(sketch, "E35.4.0.0", {"center": v(8.51, 23.34) * mm, "majorRadius": 0.28 * mm, "minorRadius": 0.2 * mm, "majorAxis": v(-1, 0)});
            skEllipse(sketch, "E35.5.0.0", {"center": v(8.51, 29.51) * mm, "majorRadius": 0.28 * mm, "minorRadius": 0.2 * mm, "majorAxis": v(-1, 0)});
            skEllipse(sketch, "E35.6.0.0", {"center": v(8.51, 35.69) * mm, "majorRadius": 0.28 * mm, "minorRadius": 0.2 * mm, "majorAxis": v(-1, 0)});
            skEllipse(sketch, "E35.7.0.0", {"center": v(8.51, 41.86) * mm, "majorRadius": 0.28 * mm, "minorRadius": 0.2 * mm, "majorAxis": v(-1, 0)});
            skEllipse(sketch, "E35.8.0.0", {"center": v(8.51, 48.03) * mm, "majorRadius": 0.28 * mm, "minorRadius": 0.2 * mm, "majorAxis": v(-1, 0)});
            skEllipse(sketch, "E35.9.0.0", {"center": v(8.51, 54.2) * mm, "majorRadius": 0.28 * mm, "minorRadius": 0.2 * mm, "majorAxis": v(-1, 0)});
            skEllipse(sketch, "E35.10.0.0", {"center": v(8.51, 60.38) * mm, "majorRadius": 0.28 * mm, "minorRadius": 0.2 * mm, "majorAxis": v(-1, 0)});
            skEllipse(sketch, "E35.11.0.0", {"center": v(8.51, 66.55) * mm, "majorRadius": 0.28 * mm, "minorRadius": 0.2 * mm, "majorAxis": v(-1, 0)});
            skEllipse(sketch, "E35.12.0.0", {"center": v(8.51, 72.72) * mm, "majorRadius": 0.28 * mm, "minorRadius": 0.2 * mm, "majorAxis": v(-1, 0)});
            skEllipse(sketch, "E35.13.0.0", {"center": v(8.51, 78.9) * mm, "majorRadius": 0.28 * mm, "minorRadius": 0.2 * mm, "majorAxis": v(-1, 0)});
            skEllipse(sketch, "E35.14.0.0", {"center": v(8.51, 85.06) * mm, "majorRadius": 0.28 * mm, "minorRadius": 0.2 * mm, "majorAxis": v(-1, 0)});
            skEllipse(sketch, "E35.15.0.0", {"center": v(8.51, 91.24) * mm, "majorRadius": 0.28 * mm, "minorRadius": 0.2 * mm, "majorAxis": v(-1, 0)});
            skEllipse(sketch, "E35.16.0.0", {"center": v(8.51, 97.4) * mm, "majorRadius": 0.28 * mm, "minorRadius": 0.2 * mm, "majorAxis": v(-1, 0)});
            skEllipse(sketch, "E35.17.0.0", {"center": v(8.51, 103.58) * mm, "majorRadius": 0.28 * mm, "minorRadius": 0.2 * mm, "majorAxis": v(-1, 0)});
            skEllipse(sketch, "E35.18.0.0", {"center": v(8.51, 109.75) * mm, "majorRadius": 0.28 * mm, "minorRadius": 0.2 * mm, "majorAxis": v(-1, 0)});
            skEllipse(sketch, "E35.19.0.0", {"center": v(8.51, 115.93) * mm, "majorRadius": 0.28 * mm, "minorRadius": 0.2 * mm, "majorAxis": v(-1, 0)});
            skEllipse(sketch, "E35.20.0.0", {"center": v(8.51, 122.1) * mm, "majorRadius": 0.28 * mm, "minorRadius": 0.2 * mm, "majorAxis": v(-1, 0)});
            skEllipse(sketch, "E35.21.0.0", {"center": v(8.51, 128.27) * mm, "majorRadius": 0.28 * mm, "minorRadius": 0.2 * mm, "majorAxis": v(-1, 0)});
            skEllipse(sketch, "E35.22.0.0", {"center": v(8.51, 134.44) * mm, "majorRadius": 0.28 * mm, "minorRadius": 0.2 * mm, "majorAxis": v(-1, 0)});
            skEllipse(sketch, "E35.23.0.0", {"center": v(8.51, 140.61) * mm, "majorRadius": 0.28 * mm, "minorRadius": 0.2 * mm, "majorAxis": v(-1, 0)});
            skEllipse(sketch, "E35.24.0.0", {"center": v(8.51, 146.79) * mm, "majorRadius": 0.28 * mm, "minorRadius": 0.2 * mm, "majorAxis": v(-1, 0)});
            skEllipse(sketch, "E35.25.0.0", {"center": v(8.51, 152.96) * mm, "majorRadius": 0.28 * mm, "minorRadius": 0.2 * mm, "majorAxis": v(-1, 0)});
            skEllipse(sketch, "E35.26.0.0", {"center": v(8.51, 159.13) * mm, "majorRadius": 0.28 * mm, "minorRadius": 0.2 * mm, "majorAxis": v(-1, 0)});
            skEllipse(sketch, "E35.27.0.0", {"center": v(8.51, 165.3) * mm, "majorRadius": 0.28 * mm, "minorRadius": 0.2 * mm, "majorAxis": v(-1, 0)});
            skEllipse(sketch, "E35.28.0.0", {"center": v(8.51, 171.48) * mm, "majorRadius": 0.28 * mm, "minorRadius": 0.2 * mm, "majorAxis": v(-1, 0)});
            skEllipse(sketch, "E35.29.0.0", {"center": v(8.51, 177.65) * mm, "majorRadius": 0.28 * mm, "minorRadius": 0.2 * mm, "majorAxis": v(-1, 0)});
            skEllipse(sketch, "E35.30.0.0", {"center": v(8.51, 183.82) * mm, "majorRadius": 0.28 * mm, "minorRadius": 0.2 * mm, "majorAxis": v(-1, 0)});
            skEllipse(sketch, "E35.31.0.0", {"center": v(8.51, 190) * mm, "majorRadius": 0.28 * mm, "minorRadius": 0.2 * mm, "majorAxis": v(-1, 0)});
            skEllipse(sketch, "E35.32.0.0", {"center": v(8.51, 196.16) * mm, "majorRadius": 0.28 * mm, "minorRadius": 0.2 * mm, "majorAxis": v(-1, 0)});
            skEllipse(sketch, "E35.33.0.0", {"center": v(8.51, 202.34) * mm, "majorRadius": 0.28 * mm, "minorRadius": 0.2 * mm, "majorAxis": v(-1, 0)});
            skEllipse(sketch, "E35.34.0.0", {"center": v(8.51, 208.5) * mm, "majorRadius": 0.28 * mm, "minorRadius": 0.2 * mm, "majorAxis": v(-1, 0)});
            skEllipse(sketch, "E35.35.0.0", {"center": v(8.51, 214.68) * mm, "majorRadius": 0.28 * mm, "minorRadius": 0.2 * mm, "majorAxis": v(-1, 0)});
            skEllipse(sketch, "E35.36.0.0", {"center": v(8.51, 220.85) * mm, "majorRadius": 0.28 * mm, "minorRadius": 0.2 * mm, "majorAxis": v(-1, 0)});
            skLineSegment(sketch, "E35.direction1", {"start": v(8.51, -1.35) * mm, "end": v(8.51, 4.83) * mm, "construction": true});
            skSolve(sketch);
        }
        {
            var Q0;
            Q0 = qSketchRegion(id + "F7", true);
            extrude(context, id + "F8", {"entities" : qUnion([Q0]), "operationType" : NewBodyOperationType.ADD, "depth" : 0.25 * mm, "hasSecondDirection" : true, "secondDirectionOppositeDirection" : true, "secondDirectionDepth" : 0.5 * mm});
        }
        {
            var Q0;
            Q0=makeQuery(id+"F4.opExtrude","SWEPT_FACE",FACE,{"disambiguationData":[OSD([sQuery(id+"F3.wireOp",EDGE,"E15.MirrorCS")])]});
            var sketch = newSketch(context, id + "F9", { "sketchPlane" : qUnion([Q0])});
            skEllipse(sketch, "E36", {"center": v(-8.63, -1.35) * mm, "majorRadius": 0.28 * mm, "minorRadius": 0.2 * mm, "majorAxis": v(1, 0)});
            skEllipse(sketch, "E37.1.0.0", {"center": v(-8.63, 4.83) * mm, "majorRadius": 0.28 * mm, "minorRadius": 0.2 * mm, "majorAxis": v(1, 0)});
            skEllipse(sketch, "E37.2.0.0", {"center": v(-8.63, 11) * mm, "majorRadius": 0.28 * mm, "minorRadius": 0.2 * mm, "majorAxis": v(1, 0)});
            skEllipse(sketch, "E37.3.0.0", {"center": v(-8.63, 17.17) * mm, "majorRadius": 0.28 * mm, "minorRadius": 0.2 * mm, "majorAxis": v(1, 0)});
            skEllipse(sketch, "E37.4.0.0", {"center": v(-8.63, 23.34) * mm, "majorRadius": 0.28 * mm, "minorRadius": 0.2 * mm, "majorAxis": v(1, 0)});
            skEllipse(sketch, "E37.5.0.0", {"center": v(-8.63, 29.51) * mm, "majorRadius": 0.28 * mm, "minorRadius": 0.2 * mm, "majorAxis": v(1, 0)});
            skEllipse(sketch, "E37.6.0.0", {"center": v(-8.63, 35.69) * mm, "majorRadius": 0.28 * mm, "minorRadius": 0.2 * mm, "majorAxis": v(1, 0)});
            skEllipse(sketch, "E37.7.0.0", {"center": v(-8.63, 41.86) * mm, "majorRadius": 0.28 * mm, "minorRadius": 0.2 * mm, "majorAxis": v(1, 0)});
            skEllipse(sketch, "E37.8.0.0", {"center": v(-8.63, 48.03) * mm, "majorRadius": 0.28 * mm, "minorRadius": 0.2 * mm, "majorAxis": v(1, 0)});
            skEllipse(sketch, "E37.9.0.0", {"center": v(-8.63, 54.2) * mm, "majorRadius": 0.28 * mm, "minorRadius": 0.2 * mm, "majorAxis": v(1, 0)});
            skEllipse(sketch, "E37.10.0.0", {"center": v(-8.63, 60.38) * mm, "majorRadius": 0.28 * mm, "minorRadius": 0.2 * mm, "majorAxis": v(1, 0)});
            skEllipse(sketch, "E37.11.0.0", {"center": v(-8.63, 66.55) * mm, "majorRadius": 0.28 * mm, "minorRadius": 0.2 * mm, "majorAxis": v(1, 0)});
            skEllipse(sketch, "E37.12.0.0", {"center": v(-8.63, 72.72) * mm, "majorRadius": 0.28 * mm, "minorRadius": 0.2 * mm, "majorAxis": v(1, 0)});
            skEllipse(sketch, "E37.13.0.0", {"center": v(-8.63, 78.9) * mm, "majorRadius": 0.28 * mm, "minorRadius": 0.2 * mm, "majorAxis": v(1, 0)});
            skEllipse(sketch, "E37.14.0.0", {"center": v(-8.63, 85.06) * mm, "majorRadius": 0.28 * mm, "minorRadius": 0.2 * mm, "majorAxis": v(1, 0)});
            skEllipse(sketch, "E37.15.0.0", {"center": v(-8.63, 91.24) * mm, "majorRadius": 0.28 * mm, "minorRadius": 0.2 * mm, "majorAxis": v(1, 0)});
            skEllipse(sketch, "E37.16.0.0", {"center": v(-8.63, 97.4) * mm, "majorRadius": 0.28 * mm, "minorRadius": 0.2 * mm, "majorAxis": v(1, 0)});
            skEllipse(sketch, "E37.17.0.0", {"center": v(-8.63, 103.58) * mm, "majorRadius": 0.28 * mm, "minorRadius": 0.2 * mm, "majorAxis": v(1, 0)});
            skEllipse(sketch, "E37.18.0.0", {"center": v(-8.63, 109.75) * mm, "majorRadius": 0.28 * mm, "minorRadius": 0.2 * mm, "majorAxis": v(1, 0)});
            skEllipse(sketch, "E37.19.0.0", {"center": v(-8.63, 115.93) * mm, "majorRadius": 0.28 * mm, "minorRadius": 0.2 * mm, "majorAxis": v(1, 0)});
            skEllipse(sketch, "E37.20.0.0", {"center": v(-8.63, 122.1) * mm, "majorRadius": 0.28 * mm, "minorRadius": 0.2 * mm, "majorAxis": v(1, 0)});
            skEllipse(sketch, "E37.21.0.0", {"center": v(-8.63, 128.27) * mm, "majorRadius": 0.28 * mm, "minorRadius": 0.2 * mm, "majorAxis": v(1, 0)});
            skEllipse(sketch, "E37.22.0.0", {"center": v(-8.63, 134.44) * mm, "majorRadius": 0.28 * mm, "minorRadius": 0.2 * mm, "majorAxis": v(1, 0)});
            skEllipse(sketch, "E37.23.0.0", {"center": v(-8.63, 140.61) * mm, "majorRadius": 0.28 * mm, "minorRadius": 0.2 * mm, "majorAxis": v(1, 0)});
            skEllipse(sketch, "E37.24.0.0", {"center": v(-8.63, 146.79) * mm, "majorRadius": 0.28 * mm, "minorRadius": 0.2 * mm, "majorAxis": v(1, 0)});
            skEllipse(sketch, "E37.25.0.0", {"center": v(-8.63, 152.96) * mm, "majorRadius": 0.28 * mm, "minorRadius": 0.2 * mm, "majorAxis": v(1, 0)});
            skEllipse(sketch, "E37.26.0.0", {"center": v(-8.63, 159.13) * mm, "majorRadius": 0.28 * mm, "minorRadius": 0.2 * mm, "majorAxis": v(1, 0)});
            skEllipse(sketch, "E37.27.0.0", {"center": v(-8.63, 165.3) * mm, "majorRadius": 0.28 * mm, "minorRadius": 0.2 * mm, "majorAxis": v(1, 0)});
            skEllipse(sketch, "E37.28.0.0", {"center": v(-8.63, 171.48) * mm, "majorRadius": 0.28 * mm, "minorRadius": 0.2 * mm, "majorAxis": v(1, 0)});
            skEllipse(sketch, "E37.29.0.0", {"center": v(-8.63, 177.65) * mm, "majorRadius": 0.28 * mm, "minorRadius": 0.2 * mm, "majorAxis": v(1, 0)});
            skEllipse(sketch, "E37.30.0.0", {"center": v(-8.63, 183.82) * mm, "majorRadius": 0.28 * mm, "minorRadius": 0.2 * mm, "majorAxis": v(1, 0)});
            skEllipse(sketch, "E37.31.0.0", {"center": v(-8.63, 190) * mm, "majorRadius": 0.28 * mm, "minorRadius": 0.2 * mm, "majorAxis": v(1, 0)});
            skEllipse(sketch, "E37.32.0.0", {"center": v(-8.63, 196.16) * mm, "majorRadius": 0.28 * mm, "minorRadius": 0.2 * mm, "majorAxis": v(1, 0)});
            skEllipse(sketch, "E37.33.0.0", {"center": v(-8.63, 202.34) * mm, "majorRadius": 0.28 * mm, "minorRadius": 0.2 * mm, "majorAxis": v(1, 0)});
            skEllipse(sketch, "E37.34.0.0", {"center": v(-8.63, 208.5) * mm, "majorRadius": 0.28 * mm, "minorRadius": 0.2 * mm, "majorAxis": v(1, 0)});
            skEllipse(sketch, "E37.35.0.0", {"center": v(-8.63, 214.68) * mm, "majorRadius": 0.28 * mm, "minorRadius": 0.2 * mm, "majorAxis": v(1, 0)});
            skEllipse(sketch, "E37.36.0.0", {"center": v(-8.63, 220.85) * mm, "majorRadius": 0.28 * mm, "minorRadius": 0.2 * mm, "majorAxis": v(1, 0)});
            skLineSegment(sketch, "E37.direction1", {"start": v(-8.63, -1.35) * mm, "end": v(-8.63, 4.83) * mm, "construction": true});
            skSolve(sketch);
        }
        {
            var Q0;
            Q0 = qSketchRegion(id + "F9", true);
            extrude(context, id + "F10", {"entities" : qUnion([Q0]), "operationType" : NewBodyOperationType.ADD, "depth" : 0.25 * mm, "hasSecondDirection" : true, "secondDirectionOppositeDirection" : true, "secondDirectionDepth" : 0.5 * mm});
        }
        {
            var Q0;
            Q0=makeQuery(id+"F4.opExtrude","SWEPT_FACE",FACE,{"disambiguationData":[OSD([sQuery(id+"F3.wireOp",EDGE,"E21.MirrorCS")])]});
            var sketch = newSketch(context, id + "F11", { "sketchPlane" : qUnion([Q0])});
            skEllipse(sketch, "E38", {"center": v(8.63, -1.35) * mm, "majorRadius": 0.28 * mm, "minorRadius": 0.2 * mm, "majorAxis": v(1, 0)});
            skEllipse(sketch, "E39.1.0.0", {"center": v(8.63, 4.83) * mm, "majorRadius": 0.28 * mm, "minorRadius": 0.2 * mm, "majorAxis": v(1, 0)});
            skEllipse(sketch, "E39.2.0.0", {"center": v(8.63, 11) * mm, "majorRadius": 0.28 * mm, "minorRadius": 0.2 * mm, "majorAxis": v(1, 0)});
            skEllipse(sketch, "E39.3.0.0", {"center": v(8.63, 17.17) * mm, "majorRadius": 0.28 * mm, "minorRadius": 0.2 * mm, "majorAxis": v(1, 0)});
            skEllipse(sketch, "E39.4.0.0", {"center": v(8.63, 23.34) * mm, "majorRadius": 0.28 * mm, "minorRadius": 0.2 * mm, "majorAxis": v(1, 0)});
            skEllipse(sketch, "E39.5.0.0", {"center": v(8.63, 29.51) * mm, "majorRadius": 0.28 * mm, "minorRadius": 0.2 * mm, "majorAxis": v(1, 0)});
            skEllipse(sketch, "E39.6.0.0", {"center": v(8.63, 35.69) * mm, "majorRadius": 0.28 * mm, "minorRadius": 0.2 * mm, "majorAxis": v(1, 0)});
            skEllipse(sketch, "E39.7.0.0", {"center": v(8.63, 41.86) * mm, "majorRadius": 0.28 * mm, "minorRadius": 0.2 * mm, "majorAxis": v(1, 0)});
            skEllipse(sketch, "E39.8.0.0", {"center": v(8.63, 48.03) * mm, "majorRadius": 0.28 * mm, "minorRadius": 0.2 * mm, "majorAxis": v(1, 0)});
            skEllipse(sketch, "E39.9.0.0", {"center": v(8.63, 54.2) * mm, "majorRadius": 0.28 * mm, "minorRadius": 0.2 * mm, "majorAxis": v(1, 0)});
            skEllipse(sketch, "E39.10.0.0", {"center": v(8.63, 60.38) * mm, "majorRadius": 0.28 * mm, "minorRadius": 0.2 * mm, "majorAxis": v(1, 0)});
            skEllipse(sketch, "E39.11.0.0", {"center": v(8.63, 66.55) * mm, "majorRadius": 0.28 * mm, "minorRadius": 0.2 * mm, "majorAxis": v(1, 0)});
            skEllipse(sketch, "E39.12.0.0", {"center": v(8.63, 72.72) * mm, "majorRadius": 0.28 * mm, "minorRadius": 0.2 * mm, "majorAxis": v(1, 0)});
            skEllipse(sketch, "E39.13.0.0", {"center": v(8.63, 78.9) * mm, "majorRadius": 0.28 * mm, "minorRadius": 0.2 * mm, "majorAxis": v(1, 0)});
            skEllipse(sketch, "E39.14.0.0", {"center": v(8.63, 85.06) * mm, "majorRadius": 0.28 * mm, "minorRadius": 0.2 * mm, "majorAxis": v(1, 0)});
            skEllipse(sketch, "E39.15.0.0", {"center": v(8.63, 91.24) * mm, "majorRadius": 0.28 * mm, "minorRadius": 0.2 * mm, "majorAxis": v(1, 0)});
            skEllipse(sketch, "E39.16.0.0", {"center": v(8.63, 97.4) * mm, "majorRadius": 0.28 * mm, "minorRadius": 0.2 * mm, "majorAxis": v(1, 0)});
            skEllipse(sketch, "E39.17.0.0", {"center": v(8.63, 103.58) * mm, "majorRadius": 0.28 * mm, "minorRadius": 0.2 * mm, "majorAxis": v(1, 0)});
            skEllipse(sketch, "E39.18.0.0", {"center": v(8.63, 109.75) * mm, "majorRadius": 0.28 * mm, "minorRadius": 0.2 * mm, "majorAxis": v(1, 0)});
            skEllipse(sketch, "E39.19.0.0", {"center": v(8.63, 115.93) * mm, "majorRadius": 0.28 * mm, "minorRadius": 0.2 * mm, "majorAxis": v(1, 0)});
            skEllipse(sketch, "E39.20.0.0", {"center": v(8.63, 122.1) * mm, "majorRadius": 0.28 * mm, "minorRadius": 0.2 * mm, "majorAxis": v(1, 0)});
            skEllipse(sketch, "E39.21.0.0", {"center": v(8.63, 128.27) * mm, "majorRadius": 0.28 * mm, "minorRadius": 0.2 * mm, "majorAxis": v(1, 0)});
            skEllipse(sketch, "E39.22.0.0", {"center": v(8.63, 134.44) * mm, "majorRadius": 0.28 * mm, "minorRadius": 0.2 * mm, "majorAxis": v(1, 0)});
            skEllipse(sketch, "E39.23.0.0", {"center": v(8.63, 140.61) * mm, "majorRadius": 0.28 * mm, "minorRadius": 0.2 * mm, "majorAxis": v(1, 0)});
            skEllipse(sketch, "E39.24.0.0", {"center": v(8.63, 146.79) * mm, "majorRadius": 0.28 * mm, "minorRadius": 0.2 * mm, "majorAxis": v(1, 0)});
            skEllipse(sketch, "E39.25.0.0", {"center": v(8.63, 152.96) * mm, "majorRadius": 0.28 * mm, "minorRadius": 0.2 * mm, "majorAxis": v(1, 0)});
            skEllipse(sketch, "E39.26.0.0", {"center": v(8.63, 159.13) * mm, "majorRadius": 0.28 * mm, "minorRadius": 0.2 * mm, "majorAxis": v(1, 0)});
            skEllipse(sketch, "E39.27.0.0", {"center": v(8.63, 165.3) * mm, "majorRadius": 0.28 * mm, "minorRadius": 0.2 * mm, "majorAxis": v(1, 0)});
            skEllipse(sketch, "E39.28.0.0", {"center": v(8.63, 171.48) * mm, "majorRadius": 0.28 * mm, "minorRadius": 0.2 * mm, "majorAxis": v(1, 0)});
            skEllipse(sketch, "E39.29.0.0", {"center": v(8.63, 177.65) * mm, "majorRadius": 0.28 * mm, "minorRadius": 0.2 * mm, "majorAxis": v(1, 0)});
            skEllipse(sketch, "E39.30.0.0", {"center": v(8.63, 183.82) * mm, "majorRadius": 0.28 * mm, "minorRadius": 0.2 * mm, "majorAxis": v(1, 0)});
            skEllipse(sketch, "E39.31.0.0", {"center": v(8.63, 190) * mm, "majorRadius": 0.28 * mm, "minorRadius": 0.2 * mm, "majorAxis": v(1, 0)});
            skEllipse(sketch, "E39.32.0.0", {"center": v(8.63, 196.16) * mm, "majorRadius": 0.28 * mm, "minorRadius": 0.2 * mm, "majorAxis": v(1, 0)});
            skEllipse(sketch, "E39.33.0.0", {"center": v(8.63, 202.34) * mm, "majorRadius": 0.28 * mm, "minorRadius": 0.2 * mm, "majorAxis": v(1, 0)});
            skEllipse(sketch, "E39.34.0.0", {"center": v(8.63, 208.5) * mm, "majorRadius": 0.28 * mm, "minorRadius": 0.2 * mm, "majorAxis": v(1, 0)});
            skEllipse(sketch, "E39.35.0.0", {"center": v(8.63, 214.68) * mm, "majorRadius": 0.28 * mm, "minorRadius": 0.2 * mm, "majorAxis": v(1, 0)});
            skEllipse(sketch, "E39.36.0.0", {"center": v(8.63, 220.85) * mm, "majorRadius": 0.28 * mm, "minorRadius": 0.2 * mm, "majorAxis": v(1, 0)});
            skLineSegment(sketch, "E39.direction1", {"start": v(8.63, -1.35) * mm, "end": v(8.63, 4.83) * mm, "construction": true});
            skSolve(sketch);
        }
        {
            var Q0;
            Q0 = qSketchRegion(id + "F11", true);
            extrude(context, id + "F12", {"entities" : qUnion([Q0]), "operationType" : NewBodyOperationType.ADD, "depth" : 0.25 * mm, "hasSecondDirection" : true, "secondDirectionOppositeDirection" : true, "secondDirectionDepth" : 0.5 * mm});
        }
    });
